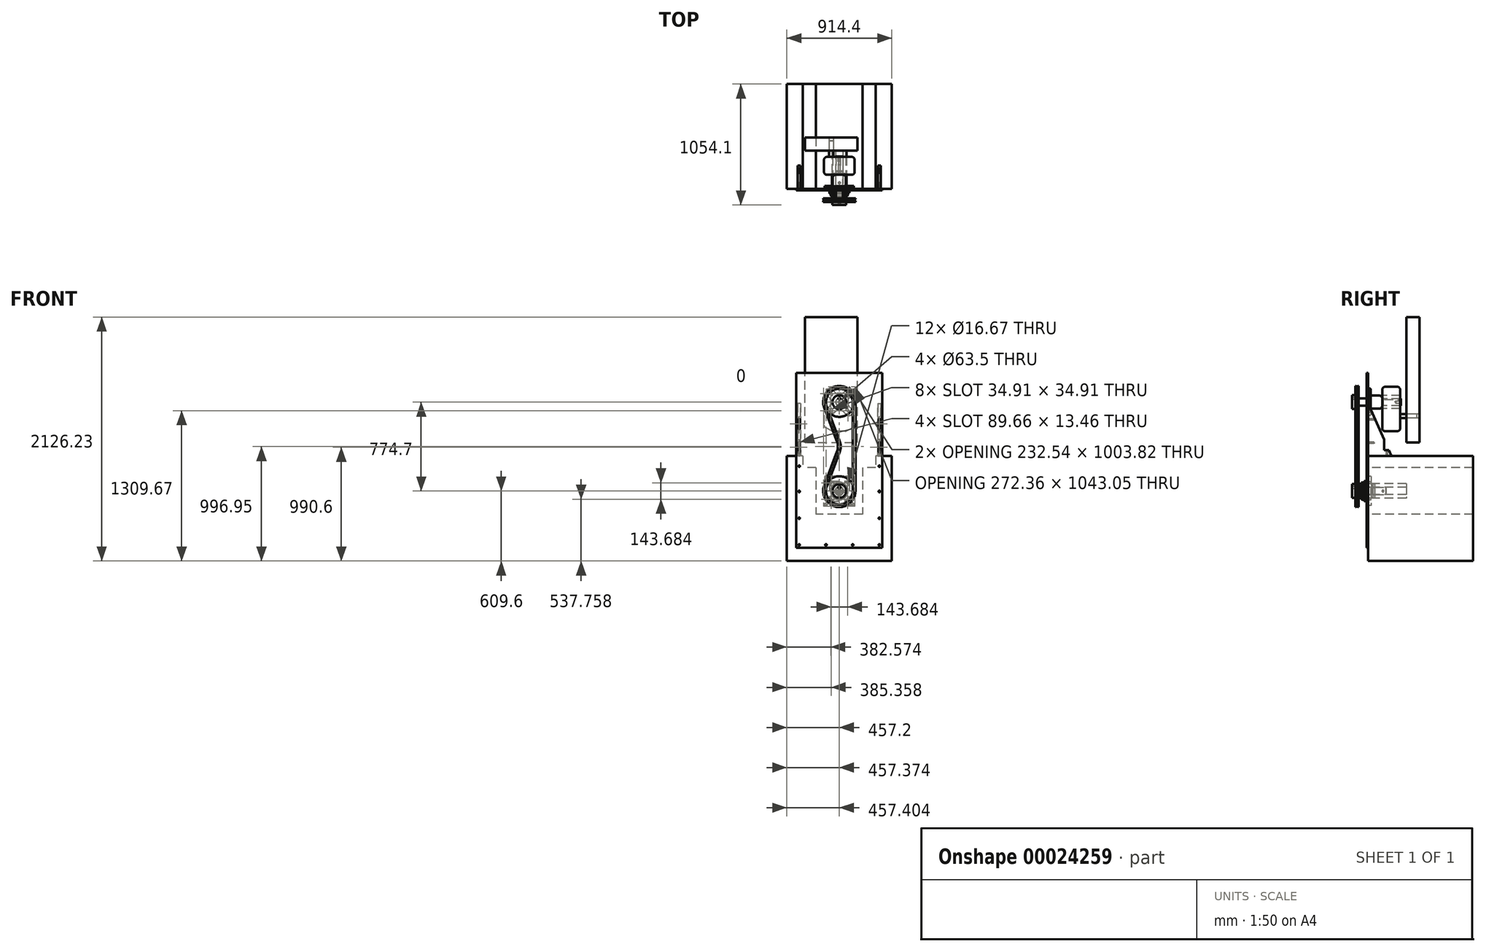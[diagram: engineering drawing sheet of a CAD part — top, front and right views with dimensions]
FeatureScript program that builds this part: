
annotation { "Feature Type Name" : "Feature", "Feature Type Description" : "" }
export const myFeature = defineFeature(function(context is Context, id is Id, definition is map)
    precondition{}
    {
        {
            var Q0;
            Q0=qCreatedBy(makeId("Front.planeOp"),FACE);
            var sketch = newSketch(context, id + "F0", { "sketchPlane" : qUnion([Q0])});
            skLineSegment(sketch, "E0.bottom", {"start": v(-374.65, 254) * mm, "end": v(374.65, 254) * mm});
            skLineSegment(sketch, "E0.top", {"start": v(-374.65, -1270) * mm, "end": v(374.65, -1270) * mm});
            skLineSegment(sketch, "E0.left", {"start": v(-374.65, 254) * mm, "end": v(-374.65, -1270) * mm});
            skLineSegment(sketch, "E0.right", {"start": v(374.65, 254) * mm, "end": v(374.65, -1270) * mm});
            skCircle(sketch, "E1", {"center": v(0, 0) * mm, "radius": 31.75 * mm});
            skCircle(sketch, "E2", {"center": v(0, -774.7) * mm, "radius": 31.75 * mm});
            skLineSegment(sketch, "E3", {"start": v(349.25, -152.4) * mm, "end": v(349.25, -228.6) * mm, "construction": true});
            skArc(sketch, "E4", {"start": v(355.98, -152.4) * mm, "mid": v(349.25, -145.67) * mm, "end": v(342.52, -152.4) * mm});
            skArc(sketch, "E5", {"start": v(342.52, -228.6) * mm, "mid": v(349.25, -235.33) * mm, "end": v(355.98, -228.6) * mm});
            skLineSegment(sketch, "E6.0", {"start": v(355.98, -152.4) * mm, "end": v(355.98, -228.6) * mm});
            skLineSegment(sketch, "E7.0", {"start": v(342.52, -152.4) * mm, "end": v(342.52, -228.6) * mm});
            skArc(sketch, "E8.0.1.0", {"start": v(355.98, -355.6) * mm, "mid": v(349.25, -348.87) * mm, "end": v(342.52, -355.6) * mm});
            skLineSegment(sketch, "E8.0.1.1", {"start": v(355.98, -355.6) * mm, "end": v(355.98, -431.8) * mm});
            skArc(sketch, "E8.0.1.2", {"start": v(342.52, -431.8) * mm, "mid": v(349.25, -438.53) * mm, "end": v(355.98, -431.8) * mm});
            skLineSegment(sketch, "E8.0.1.3", {"start": v(342.52, -355.6) * mm, "end": v(342.52, -431.8) * mm});
            skArc(sketch, "E8.1.0.0", {"start": v(-342.52, -152.4) * mm, "mid": v(-349.25, -145.67) * mm, "end": v(-355.98, -152.4) * mm});
            skLineSegment(sketch, "E8.1.0.1", {"start": v(-342.52, -152.4) * mm, "end": v(-342.52, -228.6) * mm});
            skArc(sketch, "E8.1.0.2", {"start": v(-355.98, -228.6) * mm, "mid": v(-349.25, -235.33) * mm, "end": v(-342.52, -228.6) * mm});
            skLineSegment(sketch, "E8.1.0.3", {"start": v(-355.98, -152.4) * mm, "end": v(-355.98, -228.6) * mm});
            skArc(sketch, "E8.1.1.0", {"start": v(-342.52, -355.6) * mm, "mid": v(-349.25, -348.87) * mm, "end": v(-355.98, -355.6) * mm});
            skLineSegment(sketch, "E8.1.1.1", {"start": v(-342.52, -355.6) * mm, "end": v(-342.52, -431.8) * mm});
            skArc(sketch, "E8.1.1.2", {"start": v(-355.98, -431.8) * mm, "mid": v(-349.25, -438.53) * mm, "end": v(-342.52, -431.8) * mm});
            skLineSegment(sketch, "E8.1.1.3", {"start": v(-355.98, -355.6) * mm, "end": v(-355.98, -431.8) * mm});
            skLineSegment(sketch, "E8.direction1", {"start": v(342.52, -152.4) * mm, "end": v(-355.98, -152.4) * mm, "construction": true});
            skLineSegment(sketch, "E8.direction2", {"start": v(342.52, -152.4) * mm, "end": v(342.52, -355.6) * mm, "construction": true});
            skSolve(sketch);
        }
        {
            var Q0;
            Q0=makeQuery(id+"F0.imprint","IMPRINT",FACE,{"disambiguationData":[TD([[makeQuery(id+"F0.imprint","IMPRINT",EDGE,{"derivedFrom":sQuery(id+"F0.wireOp",EDGE,"E0.bottom")}),-1.0]])]});
            extrude(context, id + "F1", {"entities" : qUnion([Q0]), "depth" : 12.7 * mm});
        }
        {
            var Q0;
            Q0=makeQuery(id+"F1.opExtrude","CAP_FACE",FACE,{"disambiguationData":[OSD([sQuery(id+"F0.wireOp",EDGE,"E0.bottom"),sQuery(id+"F0.wireOp",EDGE,"E0.top"),sQuery(id+"F0.wireOp",EDGE,"E0.left"),sQuery(id+"F0.wireOp",EDGE,"E0.right"),sQuery(id+"F0.wireOp",EDGE,"E1")])],"isStart":false});
            var sketch = newSketch(context, id + "F2", { "sketchPlane" : qUnion([Q0])});
            skCircle(sketch, "E9", {"center": v(0, 0) * mm, "radius": 92.08 * mm, "construction": true});
            skLineSegment(sketch, "E10", {"start": v(0, 0) * mm, "end": v(65.1, 65.1) * mm, "construction": true});
            skLineSegment(sketch, "E11", {"start": v(65.1, 65.1) * mm, "end": v(84.14, 84.14) * mm, "construction": true});
            skArc(sketch, "E12", {"start": v(89.76, 78.53) * mm, "mid": v(89.76, 89.76) * mm, "end": v(78.53, 89.76) * mm});
            skArc(sketch, "E13", {"start": v(59.5, 70.72) * mm, "mid": v(59.5, 59.5) * mm, "end": v(70.72, 59.5) * mm});
            skLineSegment(sketch, "E14", {"start": v(59.5, 70.72) * mm, "end": v(78.53, 89.76) * mm});
            skLineSegment(sketch, "E15", {"start": v(70.72, 59.5) * mm, "end": v(89.76, 78.53) * mm});
            skArc(sketch, "E16.1.0", {"start": v(-78.53, 89.76) * mm, "mid": v(-89.76, 89.76) * mm, "end": v(-89.76, 78.53) * mm});
            skLineSegment(sketch, "E16.1.1", {"start": v(-59.5, 70.72) * mm, "end": v(-78.53, 89.76) * mm});
            skArc(sketch, "E16.1.2", {"start": v(-70.72, 59.5) * mm, "mid": v(-59.5, 59.5) * mm, "end": v(-59.5, 70.72) * mm});
            skLineSegment(sketch, "E16.1.3", {"start": v(-70.72, 59.5) * mm, "end": v(-89.76, 78.53) * mm});
            skArc(sketch, "E16.2.0", {"start": v(-89.76, -78.53) * mm, "mid": v(-89.76, -89.76) * mm, "end": v(-78.53, -89.76) * mm});
            skLineSegment(sketch, "E16.2.1", {"start": v(-70.72, -59.5) * mm, "end": v(-89.76, -78.53) * mm});
            skArc(sketch, "E16.2.2", {"start": v(-59.5, -70.72) * mm, "mid": v(-59.5, -59.5) * mm, "end": v(-70.72, -59.5) * mm});
            skLineSegment(sketch, "E16.2.3", {"start": v(-59.5, -70.72) * mm, "end": v(-78.53, -89.76) * mm});
            skArc(sketch, "E16.3.0", {"start": v(78.53, -89.76) * mm, "mid": v(89.76, -89.76) * mm, "end": v(89.76, -78.53) * mm});
            skLineSegment(sketch, "E16.3.1", {"start": v(59.5, -70.72) * mm, "end": v(78.53, -89.76) * mm});
            skArc(sketch, "E16.3.2", {"start": v(70.72, -59.5) * mm, "mid": v(59.5, -59.5) * mm, "end": v(59.5, -70.72) * mm});
            skLineSegment(sketch, "E16.3.3", {"start": v(70.72, -59.5) * mm, "end": v(89.76, -78.53) * mm});
            skCircle(sketch, "E17.0", {"center": v(0, -774.7) * mm, "radius": 31.75 * mm});
            skCircle(sketch, "E18", {"center": v(0, -774.7) * mm, "radius": 101.6 * mm, "construction": true});
            skLineSegment(sketch, "E19", {"start": v(0, -774.7) * mm, "end": v(-71.84, -702.86) * mm, "construction": true});
            skLineSegment(sketch, "E20", {"start": v(0, -774.7) * mm, "end": v(-71.84, -846.54) * mm, "construction": true});
            skLineSegment(sketch, "E21", {"start": v(0, -774.7) * mm, "end": v(71.84, -846.54) * mm, "construction": true});
            skLineSegment(sketch, "E22", {"start": v(0, -774.7) * mm, "end": v(71.84, -702.86) * mm, "construction": true});
            skCircle(sketch, "E23", {"center": v(-71.84, -702.86) * mm, "radius": 8.33 * mm});
            skCircle(sketch, "E24", {"center": v(71.84, -702.86) * mm, "radius": 8.33 * mm});
            skCircle(sketch, "E25", {"center": v(71.84, -846.54) * mm, "radius": 8.33 * mm});
            skCircle(sketch, "E26", {"center": v(-71.84, -846.54) * mm, "radius": 8.33 * mm});
            skSolve(sketch);
        }
        {
            var Q0;
            Q0=makeQuery(id+"F2.imprint","IMPRINT",FACE,{"disambiguationData":[TD([[makeQuery(id+"F2.imprint","IMPRINT",EDGE,{"derivedFrom":sQuery(id+"F2.wireOp",EDGE,"E16.1.0")}),1.0]])]});
            var Q1;
            Q1=makeQuery(id+"F2.imprint","IMPRINT",FACE,{"disambiguationData":[TD([[makeQuery(id+"F2.imprint","IMPRINT",EDGE,{"derivedFrom":sQuery(id+"F2.wireOp",EDGE,"E12")}),1.0]])]});
            var Q2;
            Q2=makeQuery(id+"F2.imprint","IMPRINT",FACE,{"disambiguationData":[TD([[makeQuery(id+"F2.imprint","IMPRINT",EDGE,{"derivedFrom":sQuery(id+"F2.wireOp",EDGE,"E16.3.0")}),1.0]])]});
            var Q3;
            Q3=makeQuery(id+"F2.imprint","IMPRINT",FACE,{"disambiguationData":[TD([[makeQuery(id+"F2.imprint","IMPRINT",EDGE,{"derivedFrom":sQuery(id+"F2.wireOp",EDGE,"E16.2.0")}),1.0]])]});
            var Q4;
            Q4=makeQuery(id+"F2.imprint","IMPRINT",FACE,{"disambiguationData":[TD([[makeQuery(id+"F2.imprint","IMPRINT",EDGE,{"derivedFrom":sQuery(id+"F2.wireOp",EDGE,"E23")}),1.0]])]});
            var Q5;
            Q5=makeQuery(id+"F2.imprint","IMPRINT",FACE,{"disambiguationData":[TD([[makeQuery(id+"F2.imprint","IMPRINT",EDGE,{"derivedFrom":sQuery(id+"F2.wireOp",EDGE,"E24")}),1.0]])]});
            var Q6;
            Q6=makeQuery(id+"F2.imprint","IMPRINT",FACE,{"disambiguationData":[TD([[makeQuery(id+"F2.imprint","IMPRINT",EDGE,{"derivedFrom":sQuery(id+"F2.wireOp",EDGE,"E25")}),1.0]])]});
            var Q7;
            Q7=makeQuery(id+"F2.imprint","IMPRINT",FACE,{"disambiguationData":[TD([[makeQuery(id+"F2.imprint","IMPRINT",EDGE,{"derivedFrom":sQuery(id+"F2.wireOp",EDGE,"E26")}),1.0]])]});
            extrude(context, id + "F3", {"entities" : qUnion([Q0, Q1, Q2, Q3, Q4, Q5, Q6, Q7]), "operationType" : NewBodyOperationType.REMOVE, "endBound" : BoundingType.THROUGH_ALL, "oppositeDirection" : true, "depth" : 25.4 * mm});
        }
        {
            var Q0;
            Q0=makeQuery(id+"F1.opExtrude","CAP_FACE",FACE,{"disambiguationData":[OSD([sQuery(id+"F0.wireOp",EDGE,"E0.bottom"),sQuery(id+"F0.wireOp",EDGE,"E0.top"),sQuery(id+"F0.wireOp",EDGE,"E0.left"),sQuery(id+"F0.wireOp",EDGE,"E0.right"),sQuery(id+"F0.wireOp",EDGE,"E1")])],"isStart":false});
            var sketch = newSketch(context, id + "F4", { "sketchPlane" : qUnion([Q0])});
            skLineSegment(sketch, "E27", {"start": v(-349.25, -1244.6) * mm, "end": v(-349.25, -1011.68) * mm});
            skLineSegment(sketch, "E28", {"start": v(-349.25, -1011.68) * mm, "end": v(-349.25, -778.76) * mm});
            skLineSegment(sketch, "E29", {"start": v(-349.25, -778.76) * mm, "end": v(-349.25, -558.55) * mm});
            skLineSegment(sketch, "E30", {"start": v(-349.25, -1244.6) * mm, "end": v(-116.42, -1244.6) * mm});
            skLineSegment(sketch, "E31", {"start": v(-116.42, -1244.6) * mm, "end": v(116.42, -1244.6) * mm});
            skLineSegment(sketch, "E32", {"start": v(116.42, -1244.6) * mm, "end": v(349.25, -1244.6) * mm});
            skLineSegment(sketch, "E33", {"start": v(349.25, -1244.6) * mm, "end": v(349.25, -1011.68) * mm});
            skLineSegment(sketch, "E34", {"start": v(349.25, -1011.68) * mm, "end": v(349.25, -778.76) * mm});
            skLineSegment(sketch, "E35", {"start": v(349.25, -778.76) * mm, "end": v(349.25, -558.55) * mm});
            skSolve(sketch);
        }
        {
            var Q0;
            Q0=makeQuery(id+"F1.opExtrude","CAP_FACE",FACE,{"disambiguationData":[OSD([sQuery(id+"F0.wireOp",EDGE,"E0.bottom"),sQuery(id+"F0.wireOp",EDGE,"E0.top"),sQuery(id+"F0.wireOp",EDGE,"E0.left"),sQuery(id+"F0.wireOp",EDGE,"E0.right"),sQuery(id+"F0.wireOp",EDGE,"E1"),sQuery(id+"F0.wireOp",EDGE,"E2")])],"isStart":true});
            var sketch = newSketch(context, id + "F5", { "sketchPlane" : qUnion([Q0])});
            skLineSegment(sketch, "E36.bottom", {"start": v(-457.2, -469.9) * mm, "end": v(-317.5, -469.9) * mm});
            skLineSegment(sketch, "E36.top", {"start": v(-457.2, -1384.3) * mm, "end": v(457.2, -1384.3) * mm});
            skLineSegment(sketch, "E36.left", {"start": v(-457.2, -469.9) * mm, "end": v(-457.2, -1384.3) * mm});
            skLineSegment(sketch, "E36.right", {"start": v(457.2, -469.9) * mm, "end": v(457.2, -1384.3) * mm});
            skLineSegment(sketch, "E37.top", {"start": v(-317.5, -571.5) * mm, "end": v(-203.2, -571.5) * mm});
            skLineSegment(sketch, "E37.left", {"start": v(-317.5, -469.9) * mm, "end": v(-317.5, -571.5) * mm});
            skLineSegment(sketch, "E37.right", {"start": v(317.5, -469.9) * mm, "end": v(317.5, -571.5) * mm});
            skLineSegment(sketch, "E38.top", {"start": v(-203.2, -977.9) * mm, "end": v(203.2, -977.9) * mm});
            skLineSegment(sketch, "E38.left", {"start": v(-203.2, -571.5) * mm, "end": v(-203.2, -977.9) * mm});
            skLineSegment(sketch, "E38.right", {"start": v(203.2, -571.5) * mm, "end": v(203.2, -977.9) * mm});
            skCircle(sketch, "E39.0", {"center": v(0, -774.7) * mm, "radius": 31.75 * mm});
            skLineSegment(sketch, "E40.trimOffspring", {"start": v(317.5, -469.9) * mm, "end": v(457.2, -469.9) * mm});
            skLineSegment(sketch, "E41.trimOffspring", {"start": v(203.2, -571.5) * mm, "end": v(317.5, -571.5) * mm});
            skSolve(sketch);
        }
        {
            var Q0;
            Q0=sQuery(id+"F4.wireOp",VERTEX,"E35.end");
            var Q1;
            Q1=sQuery(id+"F4.wireOp",VERTEX,"E34.end");
            var Q2;
            Q2=sQuery(id+"F4.wireOp",VERTEX,"E34.start");
            var Q3;
            Q3=sQuery(id+"F4.wireOp",VERTEX,"E33.start");
            var Q4;
            Q4=sQuery(id+"F4.wireOp",VERTEX,"E32.start");
            var Q5;
            Q5=sQuery(id+"F4.wireOp",VERTEX,"E31.start");
            var Q6;
            Q6=sQuery(id+"F4.wireOp",VERTEX,"E30.start");
            var Q7;
            Q7=sQuery(id+"F4.wireOp",VERTEX,"E28.start");
            var Q8;
            Q8=sQuery(id+"F4.wireOp",VERTEX,"E29.start");
            var Q9;
            Q9=sQuery(id+"F4.wireOp",VERTEX,"E29.end");
            var Q10;
            Q10=makeQuery(id+"F1.opExtrude","SWEPT_BODY",BODY,{"disambiguationData":[OSD([sQuery(id+"F0.wireOp",EDGE,"E0.bottom"),sQuery(id+"F0.wireOp",EDGE,"E0.top"),sQuery(id+"F0.wireOp",EDGE,"E0.left"),sQuery(id+"F0.wireOp",EDGE,"E0.right"),sQuery(id+"F0.wireOp",EDGE,"E1")])]});
            var Q11;
            Q11=makeQuery(id+"FvwLGu1whnin5f6_1.opExtrude","SWEPT_BODY",BODY,{"disambiguationData":[OSD([sQuery(id+"FVkMqshP1JO17wh_1.wireOp",EDGE,"2159b873-7c23-46c0-a165-757411d00fcc.bottom"),sQuery(id+"FVkMqshP1JO17wh_1.wireOp",EDGE,"2159b873-7c23-46c0-a165-757411d00fcc.left"),sQuery(id+"FVkMqshP1JO17wh_1.wireOp",EDGE,"2159b873-7c23-46c0-a165-757411d00fcc.right"),sQuery(id+"FVkMqshP1JO17wh_1.wireOp",EDGE,"24cee0b0-9293-4e35-ae33-5d15161a7884"),sQuery(id+"FVkMqshP1JO17wh_1.wireOp",EDGE,"e78e265b-dc5b-44fe-aaf9-1faecd1ba932"),sQuery(id+"FVkMqshP1JO17wh_1.wireOp",EDGE,"51ab0597-e32d-4c84-8225-5ee1c56d9c90"),sQuery(id+"FVkMqshP1JO17wh_1.wireOp",EDGE,"ce015651-3a30-42d7-9bac-c5efad851505"),sQuery(id+"FVkMqshP1JO17wh_1.wireOp",EDGE,"805c59fc-a44f-49e7-a92e-07f28f15a35c.top"),sQuery(id+"FVkMqshP1JO17wh_1.wireOp",EDGE,"805c59fc-a44f-49e7-a92e-07f28f15a35c.left"),sQuery(id+"FVkMqshP1JO17wh_1.wireOp",EDGE,"805c59fc-a44f-49e7-a92e-07f28f15a35c.right"),sQuery(id+"FVkMqshP1JO17wh_1.wireOp",EDGE,"c6b7b8a5-442b-4015-a9d0-dc06ce9f7f00"),sQuery(id+"FVkMqshP1JO17wh_1.wireOp",EDGE,"5b3478ee-b074-467e-b26d-c07e6315da08.trimOffspring")])]});
            hole(context, id + "F6", {"style" : HoleStyle.SIMPLE, "holeDiameter" : 13.46 * mm, "endStyle" : HoleEndStyle.BLIND, "holeDepth" : 76.2 * mm, "locations" : qUnion([Q0, Q1, Q2, Q3, Q4, Q5, Q6, Q7, Q8, Q9]), "scope" : qUnion([Q10, Q11])});
        }
        {
            var Q0;
            Q0=makeQuery(id+"F5.imprint","IMPRINT",FACE,{"disambiguationData":[TD([[makeQuery(id+"F5.imprint","IMPRINT",EDGE,{"derivedFrom":sQuery(id+"F5.wireOp",EDGE,"E36.top")}),1.0]])]});
            var Q1;
            Q1=makeQuery(id+"F5.imprint","IMPRINT",FACE,{"disambiguationData":[TD([[makeQuery(id+"F5.imprint","IMPRINT",EDGE,{"derivedFrom":sQuery(id+"F5.wireOp",EDGE,"E37.top")}),-1.0]])]});
            extrude(context, id + "F7", {"entities" : qUnion([Q0, Q1]), "depth" : 914.4 * mm});
        }
        {
            var Q0;
            Q0=makeQuery(id+"F1.opExtrude","CAP_FACE",FACE,{"disambiguationData":[OSD([sQuery(id+"F0.wireOp",EDGE,"E0.bottom"),sQuery(id+"F0.wireOp",EDGE,"E0.top"),sQuery(id+"F0.wireOp",EDGE,"E0.left"),sQuery(id+"F0.wireOp",EDGE,"E0.right"),sQuery(id+"F0.wireOp",EDGE,"E1"),sQuery(id+"F0.wireOp",EDGE,"E2")])],"isStart":true});
            var sketch = newSketch(context, id + "F8", { "sketchPlane" : qUnion([Q0])});
            skLineSegment(sketch, "E42.bottom", {"start": v(-127, -647.7) * mm, "end": v(127, -647.7) * mm});
            skLineSegment(sketch, "E42.top", {"start": v(-127, -901.7) * mm, "end": v(127, -901.7) * mm});
            skLineSegment(sketch, "E42.left", {"start": v(-127, -647.7) * mm, "end": v(-127, -901.7) * mm});
            skLineSegment(sketch, "E42.right", {"start": v(127, -647.7) * mm, "end": v(127, -901.7) * mm});
            skCircle(sketch, "E43.0", {"center": v(-71.84, -702.86) * mm, "radius": 8.33 * mm});
            skCircle(sketch, "E44.0", {"center": v(0, -774.7) * mm, "radius": 31.75 * mm});
            skCircle(sketch, "E45.0", {"center": v(71.84, -702.86) * mm, "radius": 8.33 * mm});
            skCircle(sketch, "E46.0", {"center": v(71.84, -846.54) * mm, "radius": 8.33 * mm});
            skCircle(sketch, "E47.0", {"center": v(-71.84, -846.54) * mm, "radius": 8.33 * mm});
            skSolve(sketch);
        }
        {
            var Q0;
            Q0=makeQuery(id+"F8.imprint","IMPRINT",FACE,{"disambiguationData":[TD([[makeQuery(id+"F8.imprint","IMPRINT",EDGE,{"derivedFrom":sQuery(id+"F8.wireOp",EDGE,"E42.bottom")}),-1.0]])]});
            extrude(context, id + "F9", {"entities" : qUnion([Q0]), "depth" : 25.4 * mm});
        }
        {
            var Q0;
            Q0=makeQuery(id+"F1.opExtrude","CAP_FACE",FACE,{"disambiguationData":[OSD([sQuery(id+"F0.wireOp",EDGE,"E0.bottom"),sQuery(id+"F0.wireOp",EDGE,"E0.top"),sQuery(id+"F0.wireOp",EDGE,"E0.left"),sQuery(id+"F0.wireOp",EDGE,"E0.right"),sQuery(id+"F0.wireOp",EDGE,"E1"),sQuery(id+"F0.wireOp",EDGE,"E2")])],"isStart":false});
            var sketch = newSketch(context, id + "F10", { "sketchPlane" : qUnion([Q0])});
            skCircle(sketch, "E48.0", {"center": v(0, -774.7) * mm, "radius": 31.75 * mm});
            skCircle(sketch, "E49", {"center": v(0, -774.7) * mm, "radius": 30.92 * mm});
            skSolve(sketch);
        }
        {
            var Q0;
            Q0=makeQuery(id+"F10.imprint","IMPRINT",FACE,{"disambiguationData":[TD([[makeQuery(id+"F10.imprint","IMPRINT",EDGE,{"derivedFrom":sQuery(id+"F10.wireOp",EDGE,"E49")}),1.0]])]});
            extrude(context, id + "F11", {"entities" : qUnion([Q0]), "depth" : 127 * mm});
        }
        {
            var Q0;
            Q0=makeQuery(id+"F1.opExtrude","SWEPT_FACE",FACE,{"disambiguationData":[OSD([sQuery(id+"F0.wireOp",EDGE,"E0.top")])]});
            cPlane(context, id + "F12", {"entities" : qUnion([Q0]), "cplaneType" : CPlaneType.OFFSET, "offset" : 526.26 * mm, "oppositeDirection" : true, "width" : 152.4 * mm, "height" : 152.4 * mm});
        }
        {
            var Q0;
            Q0=qCreatedBy(id+"F12.planeOp",FACE);
            var sketch = newSketch(context, id + "F13", { "sketchPlane" : qUnion([Q0])});
            skLineSegment(sketch, "E50", {"start": v(-30.92, 12.7) * mm, "end": v(-30.92, 165.1) * mm});
            skLineSegment(sketch, "E51", {"start": v(30.92, 165.1) * mm, "end": v(30.92, 12.7) * mm});
            skLineSegment(sketch, "E52.bottom", {"start": v(7.94, 165.1) * mm, "end": v(-7.94, 165.1) * mm});
            skLineSegment(sketch, "E52.left", {"start": v(7.94, 165.1) * mm, "end": v(7.94, 88.9) * mm});
            skLineSegment(sketch, "E52.right", {"start": v(-7.94, 165.1) * mm, "end": v(-7.94, 88.9) * mm});
            skArc(sketch, "E53", {"start": v(-7.94, 88.9) * mm, "mid": v(0, 80.96) * mm, "end": v(7.94, 88.9) * mm});
            skSolve(sketch);
        }
        {
            var Q0;
            Q0=makeQuery(id+"F13.imprint","IMPRINT",FACE,{"disambiguationData":[TD([[makeQuery(id+"F13.imprint","IMPRINT",EDGE,{"derivedFrom":sQuery(id+"F13.wireOp",EDGE,"E52.bottom")}),1.0]])]});
            extrude(context, id + "F14", {"entities" : qUnion([Q0]), "operationType" : NewBodyOperationType.REMOVE, "depth" : 8.3 * mm});
        }
        {
            var Q0;
            Q0=makeQuery(id+"F11.opExtrude","CAP_FACE",FACE,{"disambiguationData":[OSD([sQuery(id+"F10.wireOp",EDGE,"E49")])],"isStart":true});
            extrude(context, id + "F15", {"entities" : qUnion([Q0]), "operationType" : NewBodyOperationType.ADD, "depth" : 168.27 * mm});
        }
        {
            var Q0;
            Q0=makeQuery(id+"F9.opExtrude","SWEPT_FACE",FACE,{"disambiguationData":[OSD([sQuery(id+"F8.wireOp",EDGE,"E42.left")])]});
            cPlane(context, id + "F16", {"entities" : qUnion([Q0]), "cplaneType" : CPlaneType.OFFSET, "offset" : 0 * mm, "width" : 152.4 * mm, "height" : 152.4 * mm});
        }
        {
            var Q0;
            Q0=makeQuery(id+"F9.opExtrude","SWEPT_FACE",FACE,{"disambiguationData":[OSD([sQuery(id+"F8.wireOp",EDGE,"E42.bottom")])]});
            cPlane(context, id + "F17", {"entities" : qUnion([Q0]), "cplaneType" : CPlaneType.OFFSET, "offset" : 0 * mm, "width" : 152.4 * mm, "height" : 152.4 * mm});
        }
        {
            var Q0;
            Q0=makeQuery(id+"F9.opExtrude","CAP_FACE",FACE,{"disambiguationData":[OSD([sQuery(id+"F8.wireOp",EDGE,"E42.bottom"),sQuery(id+"F8.wireOp",EDGE,"E42.top"),sQuery(id+"F8.wireOp",EDGE,"E42.left"),sQuery(id+"F8.wireOp",EDGE,"E42.right"),sQuery(id+"F8.wireOp",EDGE,"E43.0"),sQuery(id+"F8.wireOp",EDGE,"E44.0"),sQuery(id+"F8.wireOp",EDGE,"E45.0"),sQuery(id+"F8.wireOp",EDGE,"E46.0"),sQuery(id+"F8.wireOp",EDGE,"E47.0")])],"isStart":false});
            cPlane(context, id + "F18", {"entities" : qUnion([Q0]), "cplaneType" : CPlaneType.OFFSET, "offset" : 3.17 * mm, "width" : 152.4 * mm, "height" : 152.4 * mm});
        }
        {
            var Q0;
            Q0=qCreatedBy(id+"F18.planeOp",FACE);
            var sketch = newSketch(context, id + "F19", { "sketchPlane" : qUnion([Q0])});
            skCircle(sketch, "E54", {"center": v(0, -774.7) * mm, "radius": 63.5 * mm});
            skCircle(sketch, "E55.0", {"center": v(0, -774.7) * mm, "radius": 31.75 * mm});
            skSolve(sketch);
        }
        {
            var Q0;
            Q0=makeQuery(id+"F19.imprint","IMPRINT",FACE,{"disambiguationData":[TD([[makeQuery(id+"F19.imprint","IMPRINT",EDGE,{"derivedFrom":sQuery(id+"F19.wireOp",EDGE,"E54")}),1.0]])]});
            extrude(context, id + "F20", {"entities" : qUnion([Q0]), "depth" : 304.8 * mm});
        }
        {
            var Q0;
            Q0=qCreatedBy(id+"F17.planeOp",FACE);
            var sketch = newSketch(context, id + "F21", { "sketchPlane" : qUnion([Q0])});
            skLineSegment(sketch, "E56", {"start": v(0, 0) * mm, "end": v(0, 53.98) * mm, "construction": true});
            skLineSegment(sketch, "E57.0", {"start": v(-63.5, 28.58) * mm, "end": v(63.5, 28.58) * mm});
            skSolve(sketch);
        }
        {
            var Q0;
            Q0=qCreatedBy(id+"F16.planeOp",FACE);
            var sketch = newSketch(context, id + "F22", { "sketchPlane" : qUnion([Q0])});
            skLineSegment(sketch, "E58.0", {"start": v(28.58, -711.2) * mm, "end": v(28.58, -838.2) * mm});
            skLineSegment(sketch, "E59", {"start": v(28.58, -774.7) * mm, "end": v(130.18, -774.7) * mm});
            skSolve(sketch);
        }
        {
            var Q0;
            Q0=makeQuery(id+"F1.opExtrude","CAP_FACE",FACE,{"disambiguationData":[OSD([sQuery(id+"F0.wireOp",EDGE,"E0.bottom"),sQuery(id+"F0.wireOp",EDGE,"E0.top"),sQuery(id+"F0.wireOp",EDGE,"E0.left"),sQuery(id+"F0.wireOp",EDGE,"E0.right"),sQuery(id+"F0.wireOp",EDGE,"E1"),sQuery(id+"F0.wireOp",EDGE,"E2")])],"isStart":false});
            var sketch = newSketch(context, id + "F23", { "sketchPlane" : qUnion([Q0])});
            skLineSegment(sketch, "E60.bottom", {"start": v(-87.5, -687.2) * mm, "end": v(87.5, -687.2) * mm});
            skLineSegment(sketch, "E60.top", {"start": v(-87.5, -862.2) * mm, "end": v(87.5, -862.2) * mm});
            skLineSegment(sketch, "E60.left", {"start": v(-87.5, -687.2) * mm, "end": v(-87.5, -862.2) * mm});
            skLineSegment(sketch, "E60.right", {"start": v(87.5, -687.2) * mm, "end": v(87.5, -862.2) * mm});
            skCircle(sketch, "E61.0", {"center": v(0, -774.7) * mm, "radius": 31.75 * mm});
            skSolve(sketch);
        }
        {
            var Q0;
            Q0=makeQuery(id+"F23.imprint","IMPRINT",FACE,{"disambiguationData":[TD([[makeQuery(id+"F23.imprint","IMPRINT",EDGE,{"derivedFrom":sQuery(id+"F23.wireOp",EDGE,"E60.bottom")}),-1.0]])]});
            extrude(context, id + "F24", {"entities" : qUnion([Q0]), "depth" : 18 * mm});
        }
        {
            var Q0;
            Q0=makeQuery(id+"F24.opExtrude","SWEPT_EDGE",EDGE,{"disambiguationData":[OSD([sQuery(id+"F23.wireOp",EDGE,"E60.bottom"),sQuery(id+"F23.wireOp",EDGE,"E60.right")])]});
            var Q1;
            Q1=makeQuery(id+"F24.opExtrude","SWEPT_EDGE",EDGE,{"disambiguationData":[OSD([sQuery(id+"F23.wireOp",EDGE,"E60.bottom"),sQuery(id+"F23.wireOp",EDGE,"E60.left")])]});
            var Q2;
            Q2=makeQuery(id+"F24.opExtrude","SWEPT_EDGE",EDGE,{"disambiguationData":[OSD([sQuery(id+"F23.wireOp",EDGE,"E60.top"),sQuery(id+"F23.wireOp",EDGE,"E60.right")])]});
            var Q3;
            Q3=makeQuery(id+"F24.opExtrude","SWEPT_EDGE",EDGE,{"disambiguationData":[OSD([sQuery(id+"F23.wireOp",EDGE,"E60.top"),sQuery(id+"F23.wireOp",EDGE,"E60.left")])]});
            fillet(context, id + "F25", {"entities" : qUnion([Q0, Q1, Q2, Q3]), "radius" : 15.88 * mm, "tangentPropagation" : true, "allowEdgeOverflow" : false});
        }
        {
            var Q0;
            Q0=makeQuery(id+"F24.opExtrude","CAP_FACE",FACE,{"disambiguationData":[OSD([sQuery(id+"F2.wireOp",EDGE,"E23"),sQuery(id+"F2.wireOp",EDGE,"E24"),sQuery(id+"F2.wireOp",EDGE,"E25"),sQuery(id+"F2.wireOp",EDGE,"E26"),sQuery(id+"F23.wireOp",EDGE,"E60.bottom"),sQuery(id+"F23.wireOp",EDGE,"E60.top"),sQuery(id+"F23.wireOp",EDGE,"E60.left"),sQuery(id+"F23.wireOp",EDGE,"E60.right"),sQuery(id+"F23.wireOp",EDGE,"E61.0")])],"isStart":false});
            var sketch = newSketch(context, id + "F26", { "sketchPlane" : qUnion([Q0])});
            skCircle(sketch, "E62", {"center": v(0, -774.7) * mm, "radius": 76.2 * mm});
            skCircle(sketch, "E63.0", {"center": v(0, -774.7) * mm, "radius": 31.75 * mm});
            skSolve(sketch);
        }
        {
            var Q0;
            Q0=makeQuery(id+"F24.opExtrude","CAP_FACE",FACE,{"disambiguationData":[OSD([sQuery(id+"F2.wireOp",EDGE,"E23"),sQuery(id+"F2.wireOp",EDGE,"E24"),sQuery(id+"F2.wireOp",EDGE,"E25"),sQuery(id+"F2.wireOp",EDGE,"E26"),sQuery(id+"F23.wireOp",EDGE,"E60.bottom"),sQuery(id+"F23.wireOp",EDGE,"E60.top"),sQuery(id+"F23.wireOp",EDGE,"E60.left"),sQuery(id+"F23.wireOp",EDGE,"E60.right"),sQuery(id+"F23.wireOp",EDGE,"E61.0")])],"isStart":false});
            var sketch = newSketch(context, id + "F27", { "sketchPlane" : qUnion([Q0])});
            skLineSegment(sketch, "E64.0.0", {"start": v(71.63, -687.2) * mm, "end": v(-71.63, -687.2) * mm});
            skArc(sketch, "E64.0.1", {"start": v(-71.63, -687.2) * mm, "mid": v(-82.85, -691.85) * mm, "end": v(-87.5, -703.08) * mm});
            skLineSegment(sketch, "E64.0.2", {"start": v(-87.5, -703.08) * mm, "end": v(-87.5, -846.33) * mm});
            skArc(sketch, "E64.0.3", {"start": v(-87.5, -846.33) * mm, "mid": v(-82.85, -857.55) * mm, "end": v(-71.63, -862.2) * mm});
            skLineSegment(sketch, "E64.0.4", {"start": v(-71.63, -862.2) * mm, "end": v(71.62, -862.2) * mm});
            skArc(sketch, "E64.0.5", {"start": v(71.62, -862.2) * mm, "mid": v(82.85, -857.55) * mm, "end": v(87.5, -846.33) * mm});
            skLineSegment(sketch, "E64.0.6", {"start": v(87.5, -846.33) * mm, "end": v(87.5, -703.08) * mm});
            skArc(sketch, "E64.0.7", {"start": v(87.5, -703.08) * mm, "mid": v(82.85, -691.85) * mm, "end": v(71.63, -687.2) * mm});
            skArc(sketch, "E65", {"start": v(-62.52, -690.07) * mm, "mid": v(-82.85, -691.85) * mm, "end": v(-84.63, -712.18) * mm});
            skArc(sketch, "E66", {"start": v(84.63, -712.18) * mm, "mid": v(82.6, -691.61) * mm, "end": v(61.98, -690.47) * mm});
            skArc(sketch, "E67", {"start": v(62.52, -859.33) * mm, "mid": v(82.85, -857.55) * mm, "end": v(84.63, -837.22) * mm});
            skArc(sketch, "E68", {"start": v(-84.63, -837.22) * mm, "mid": v(-82.85, -857.55) * mm, "end": v(-62.52, -859.33) * mm});
            skCircle(sketch, "E69.0", {"center": v(0, -774.7) * mm, "radius": 31.75 * mm});
            skCircle(sketch, "E70", {"center": v(0, -774.7) * mm, "radius": 50.8 * mm});
            skLineSegment(sketch, "E71", {"start": v(-84.63, -712.18) * mm, "end": v(-49.33, -762.59) * mm});
            skLineSegment(sketch, "E72", {"start": v(-62.52, -690.07) * mm, "end": v(-12.11, -725.37) * mm});
            skLineSegment(sketch, "E73", {"start": v(15.24, -726.24) * mm, "end": v(61.98, -690.47) * mm});
            skLineSegment(sketch, "E74", {"start": v(84.63, -712.18) * mm, "end": v(49.33, -762.59) * mm});
            skLineSegment(sketch, "E75", {"start": v(49.33, -786.81) * mm, "end": v(84.63, -837.22) * mm});
            skLineSegment(sketch, "E76", {"start": v(12.11, -824.03) * mm, "end": v(62.52, -859.33) * mm});
            skLineSegment(sketch, "E77", {"start": v(-12.11, -824.03) * mm, "end": v(-62.52, -859.33) * mm});
            skLineSegment(sketch, "E78", {"start": v(-84.63, -837.22) * mm, "end": v(-49.33, -786.81) * mm});
            skSolve(sketch);
        }
        {
            var Q0;
            {var subQ1=sQuery(id+"F27.wireOp",EDGE,"E71");Q0=makeQuery(id+"F27.imprint","IMPRINT",FACE,{"disambiguationData":[TD([[makeQuery(id+"F27.imprint","IMPRINT",EDGE,{"derivedFrom":subQ1}),1.0]])]});}
            var Q1;
            {var subQ1=sQuery(id+"F27.wireOp",EDGE,"E73");Q1=makeQuery(id+"F27.imprint","IMPRINT",FACE,{"disambiguationData":[TD([[makeQuery(id+"F27.imprint","IMPRINT",EDGE,{"derivedFrom":subQ1}),-1.0]])]});}
            var Q2;
            {var subQ1=sQuery(id+"F27.wireOp",EDGE,"E75");Q2=makeQuery(id+"F27.imprint","IMPRINT",FACE,{"disambiguationData":[TD([[makeQuery(id+"F27.imprint","IMPRINT",EDGE,{"derivedFrom":subQ1}),-1.0]])]});}
            var Q3;
            {var subQ1=sQuery(id+"F27.wireOp",EDGE,"E77");Q3=makeQuery(id+"F27.imprint","IMPRINT",FACE,{"disambiguationData":[TD([[makeQuery(id+"F27.imprint","IMPRINT",EDGE,{"derivedFrom":subQ1}),-1.0]])]});}
            extrude(context, id + "F28", {"entities" : qUnion([Q0, Q1, Q2, Q3]), "operationType" : NewBodyOperationType.ADD, "depth" : 3.17 * mm});
        }
        {
            var Q0;
            Q0=makeQuery(id+"F26.imprint","IMPRINT",FACE,{"disambiguationData":[TD([[makeQuery(id+"F26.imprint","IMPRINT",EDGE,{"derivedFrom":sQuery(id+"F26.wireOp",EDGE,"E62")}),1.0]])]});
            extrude(context, id + "F29", {"entities" : qUnion([Q0]), "operationType" : NewBodyOperationType.ADD, "depth" : 30 * mm});
        }
        {
            var Q0;
            Q0=makeQuery(id+"F29.opExtrude","CAP_EDGE",EDGE,{"disambiguationData":[OSD([sQuery(id+"F26.wireOp",EDGE,"E62")])],"isStart":false});
            chamfer(context, id + "F30", {"entities" : qUnion([Q0]), "chamferType" : ChamferType.OFFSET_ANGLE, "width" : 19.05 * mm, "oppositeDirection" : true, "angle" : 10 * degree, "tangentPropagation" : true});
        }
        {
            var Q0;
            Q0=makeQuery(id+"F29.opExtrude","CAP_FACE",FACE,{"disambiguationData":[OSD([sQuery(id+"F26.wireOp",EDGE,"E62"),sQuery(id+"F26.wireOp",EDGE,"6657c57f-e435-4148-895d-80a6e9c333fb")])],"isStart":false});
            var sketch = newSketch(context, id + "F31", { "sketchPlane" : qUnion([Q0])});
            skCircle(sketch, "E79", {"center": v(0, -774.7) * mm, "radius": 37.72 * mm});
            skCircle(sketch, "E80.0", {"center": v(0, -774.7) * mm, "radius": 31.75 * mm});
            skSolve(sketch);
        }
        {
            var Q0;
            Q0=makeQuery(id+"F31.imprint","IMPRINT",FACE,{"disambiguationData":[TD([[makeQuery(id+"F31.imprint","IMPRINT",EDGE,{"derivedFrom":sQuery(id+"F31.wireOp",EDGE,"E79")}),1.0]])]});
            extrude(context, id + "F32", {"entities" : qUnion([Q0]), "operationType" : NewBodyOperationType.ADD, "depth" : 20.7 * mm});
        }
        {
            var Q0;
            Q0=makeQuery(id+"F11.opExtrude","CAP_FACE",FACE,{"disambiguationData":[OSD([sQuery(id+"F10.wireOp",EDGE,"E49")])],"isStart":false});
            cPlane(context, id + "F33", {"entities" : qUnion([Q0]), "cplaneType" : CPlaneType.OFFSET, "offset" : 0 * mm, "oppositeDirection" : true, "width" : 152.4 * mm, "height" : 152.4 * mm});
        }
        {
            var Q0;
            Q0=qCreatedBy(id+"F33.planeOp",FACE);
            var sketch = newSketch(context, id + "F34", { "sketchPlane" : qUnion([Q0])});
            skArc(sketch, "E81.0", {"start": v(-7.94, -744.81) * mm, "mid": v(0, -805.62) * mm, "end": v(7.94, -744.81) * mm});
            skCircle(sketch, "E82", {"center": v(0, -774.7) * mm, "radius": 30.92 * mm});
            skCircle(sketch, "E83", {"center": v(0, -774.7) * mm, "radius": 60.33 * mm});
            skLineSegment(sketch, "E84", {"start": v(-7.94, -744.81) * mm, "end": v(-7.94, -736.16) * mm});
            skLineSegment(sketch, "E85", {"start": v(-7.94, -736.16) * mm, "end": v(7.94, -736.16) * mm});
            skLineSegment(sketch, "E86", {"start": v(7.94, -744.81) * mm, "end": v(7.94, -736.16) * mm});
            skSolve(sketch);
        }
        {
            var Q0;
            Q0=makeQuery(id+"F34.imprint","IMPRINT",FACE,{"disambiguationData":[TD([[makeQuery(id+"F34.imprint","IMPRINT",EDGE,{"derivedFrom":sQuery(id+"F34.wireOp",EDGE,"E83")}),1.0]])]});
            extrude(context, id + "F35", {"entities" : qUnion([Q0]), "oppositeDirection" : true, "depth" : 36.2 * mm});
        }
        {
            var Q0;
            Q0=makeQuery(id+"F35.opExtrude","CAP_FACE",FACE,{"disambiguationData":[OSD([sQuery(id+"F34.wireOp",EDGE,"E82"),sQuery(id+"F34.wireOp",EDGE,"E83"),sQuery(id+"F34.wireOp",EDGE,"E84"),sQuery(id+"F34.wireOp",EDGE,"E85"),sQuery(id+"F34.wireOp",EDGE,"E86")])],"isStart":false});
            var sketch = newSketch(context, id + "F36", { "sketchPlane" : qUnion([Q0])});
            skArc(sketch, "E87.0", {"start": v(7.94, -744.81) * mm, "mid": v(0, -805.62) * mm, "end": v(-7.94, -744.81) * mm});
            skCircle(sketch, "E88", {"center": v(0, -774.7) * mm, "radius": 30.92 * mm});
            skCircle(sketch, "E89", {"center": v(0, -774.7) * mm, "radius": 128.45 * mm});
            skSolve(sketch);
        }
        {
            var Q0;
            Q0=makeQuery(id+"F36.imprint","IMPRINT",FACE,{"disambiguationData":[TD([[makeQuery(id+"F36.imprint","IMPRINT",EDGE,{"derivedFrom":sQuery(id+"F36.wireOp",EDGE,"E89")}),1.0]])]});
            var Q1;
            Q1=makeQuery(id+"F36.imprint","IMPRINT",FACE,{"disambiguationData":[TD([[makeQuery(id+"F36.imprint","IMPRINT",EDGE,{"disambiguationData":[OD(1.0)],"derivedFrom":sQuery(id+"F36.wireOp",EDGE,"E88")}),1.0]])]});
            extrude(context, id + "F37", {"entities" : qUnion([Q0, Q1]), "operationType" : NewBodyOperationType.ADD, "depth" : 14.6 * mm});
        }
        {
            var Q0;
            Q0=qCreatedBy(makeId("Right.planeOp"),FACE);
            var sketch = newSketch(context, id + "F38", { "sketchPlane" : qUnion([Q0])});
            skLineSegment(sketch, "E90.top", {"start": v(-139.7, 30.92) * mm, "end": v(0, 30.92) * mm});
            skLineSegment(sketch, "E90.left", {"start": v(-139.7, 0) * mm, "end": v(-139.7, 30.92) * mm});
            skLineSegment(sketch, "E91.top", {"start": v(0, 34.99) * mm, "end": v(78.74, 34.99) * mm});
            skLineSegment(sketch, "E92.bottom", {"start": v(135.04, 31.05) * mm, "end": v(285.24, 31.05) * mm});
            skLineSegment(sketch, "E92.right", {"start": v(285.24, 31.05) * mm, "end": v(285.24, 0) * mm});
            skLineSegment(sketch, "E93", {"start": v(-139.7, 0) * mm, "end": v(285.24, 0) * mm});
            skLineSegment(sketch, "E94", {"start": v(0, 34.99) * mm, "end": v(0, 30.92) * mm});
            skLineSegment(sketch, "E95", {"start": v(78.74, 34.99) * mm, "end": v(135.04, 31.05) * mm});
            skSolve(sketch);
        }
        {
            var Q0;
            Q0=makeQuery(id+"F38.imprint","IMPRINT",FACE,{"disambiguationData":[TD([[makeQuery(id+"F38.imprint","IMPRINT",EDGE,{"derivedFrom":sQuery(id+"F38.wireOp",EDGE,"E90.top")}),-1.0]])]});
            var Q1;
            Q1=sQuery(id+"F38.wireOp",EDGE,"E93");
            revolve(context, id + "F39", {"entities" : qUnion([Q0]), "axis" : qUnion([Q1]), "revolveType" : RevolveType.FULL});
        }
        {
            var Q0;
            Q0=makeQuery(id+"F1.opExtrude","SWEPT_FACE",FACE,{"disambiguationData":[OSD([sQuery(id+"F0.wireOp",EDGE,"E0.bottom")])]});
            cPlane(context, id + "F40", {"entities" : qUnion([Q0]), "cplaneType" : CPlaneType.OFFSET, "offset" : 223.04 * mm, "oppositeDirection" : true, "width" : 152.4 * mm, "height" : 152.4 * mm});
        }
        {
            var Q0;
            Q0=qCreatedBy(id+"F40.planeOp",FACE);
            var sketch = newSketch(context, id + "F41", { "sketchPlane" : qUnion([Q0])});
            skArc(sketch, "E96", {"start": v(7.94, -88.9) * mm, "mid": v(0, -80.96) * mm, "end": v(-7.94, -88.9) * mm});
            skLineSegment(sketch, "E97", {"start": v(-7.94, -88.9) * mm, "end": v(-7.94, -165.1) * mm});
            skLineSegment(sketch, "E98", {"start": v(7.94, -88.9) * mm, "end": v(7.94, -165.1) * mm});
            skLineSegment(sketch, "E99", {"start": v(-7.94, -165.1) * mm, "end": v(7.94, -165.1) * mm});
            skLineSegment(sketch, "E100.0", {"start": v(30.92, -139.7) * mm, "end": v(-30.92, -139.7) * mm});
            skSolve(sketch);
        }
        {
            var Q0;
            Q0=makeQuery(id+"F41.imprint","IMPRINT",FACE,{"disambiguationData":[TD([[makeQuery(id+"F41.imprint","IMPRINT",EDGE,{"derivedFrom":sQuery(id+"F41.wireOp",EDGE,"E96")}),1.0]])]});
            extrude(context, id + "F42", {"entities" : qUnion([Q0]), "operationType" : NewBodyOperationType.REMOVE, "oppositeDirection" : true, "depth" : 8.28 * mm});
        }
        {
            var Q0;
            Q0=makeQuery(id+"F39.opRevolve","SWEPT_FACE",FACE,{"disambiguationData":[OSD([sQuery(id+"F38.wireOp",EDGE,"E92.right")])]});
            var sketch = newSketch(context, id + "F43", { "sketchPlane" : qUnion([Q0])});
            skCircle(sketch, "E101.0", {"center": v(0, 0) * mm, "radius": 31.05 * mm});
            skSolve(sketch);
        }
        {
            var Q0;
            Q0=sQuery(id+"F43.wireOp",VERTEX,"E101.0.center");
            var Q1;
            Q1=makeQuery(id+"F39.opRevolve","SWEPT_BODY",BODY,{"disambiguationData":[OSD([sQuery(id+"F38.wireOp",EDGE,"E90.top"),sQuery(id+"F38.wireOp",EDGE,"E90.left"),sQuery(id+"F38.wireOp",EDGE,"E91.top"),sQuery(id+"F38.wireOp",EDGE,"76c26d02-83df-4411-9bb0-874c510d0430"),sQuery(id+"F38.wireOp",EDGE,"E92.bottom"),sQuery(id+"F38.wireOp",EDGE,"E92.right"),sQuery(id+"F38.wireOp",EDGE,"E93"),sQuery(id+"F38.wireOp",EDGE,"E94")])]});
            hole(context, id + "F44", {"style" : HoleStyle.SIMPLE, "holeDiameter" : 20.04 * mm, "endStyle" : HoleEndStyle.BLIND, "holeDepth" : 44.45 * mm, "locations" : qUnion([Q0]), "scope" : qUnion([Q1])});
        }
        {
            var Q0;
            Q0=makeQuery(id+"F39.opRevolve","SWEPT_FACE",FACE,{"disambiguationData":[OSD([sQuery(id+"F38.wireOp",EDGE,"E90.left")])]});
            cPlane(context, id + "F45", {"entities" : qUnion([Q0]), "cplaneType" : CPlaneType.OFFSET, "offset" : 0 * mm, "oppositeDirection" : true, "width" : 152.4 * mm, "height" : 152.4 * mm});
        }
        {
            var Q0;
            Q0=qCreatedBy(id+"F45.planeOp",FACE);
            var sketch = newSketch(context, id + "F46", { "sketchPlane" : qUnion([Q0])});
            skCircle(sketch, "E102", {"center": v(0, 0) * mm, "radius": 60.33 * mm});
            skArc(sketch, "E103.0", {"start": v(-7.94, 29.89) * mm, "mid": v(0, -30.92) * mm, "end": v(7.94, 29.89) * mm});
            skLineSegment(sketch, "E104.0.1", {"start": v(-7.94, 22.68) * mm, "end": v(7.94, 22.68) * mm});
            skLineSegment(sketch, "E104.0.3", {"start": v(-7.94, 22.68) * mm, "end": v(7.94, 22.68) * mm});
            skLineSegment(sketch, "E105.0.1", {"start": v(-7.94, 29.89) * mm, "end": v(-7.94, 22.68) * mm});
            skLineSegment(sketch, "E105.0.3", {"start": v(-7.94, 22.68) * mm, "end": v(-7.94, 29.89) * mm});
            skLineSegment(sketch, "E106.0", {"start": v(7.94, 22.68) * mm, "end": v(7.94, 29.89) * mm});
            skLineSegment(sketch, "E107.top", {"start": v(-7.94, 38.55) * mm, "end": v(7.94, 38.55) * mm});
            skLineSegment(sketch, "E107.left", {"start": v(-7.94, 29.89) * mm, "end": v(-7.94, 38.55) * mm});
            skLineSegment(sketch, "E107.right", {"start": v(7.94, 29.89) * mm, "end": v(7.94, 38.55) * mm});
            skSolve(sketch);
        }
        {
            var Q0;
            Q0=makeQuery(id+"F46.imprint","IMPRINT",FACE,{"disambiguationData":[TD([[makeQuery(id+"F46.imprint","IMPRINT",EDGE,{"derivedFrom":sQuery(id+"F46.wireOp",EDGE,"E102")}),1.0]])]});
            extrude(context, id + "F47", {"entities" : qUnion([Q0]), "oppositeDirection" : true, "depth" : 36.2 * mm});
        }
        {
            var Q0;
            Q0=makeQuery(id+"F47.opExtrude","CAP_FACE",FACE,{"disambiguationData":[OSD([sQuery(id+"F46.wireOp",EDGE,"837d0a8e-7aea-41cf-886a-b62b43243ce0"),sQuery(id+"F46.wireOp",EDGE,"E102"),sQuery(id+"F46.wireOp",EDGE,"d060f684-caa2-42fc-b72d-14a0c2717916"),sQuery(id+"F46.wireOp",EDGE,"17672764-d84c-446f-9bef-e2111f265863"),sQuery(id+"F46.wireOp",EDGE,"33cdaa7a-9be0-4ddf-9e29-9c811c9cda73")])],"isStart":false});
            var sketch = newSketch(context, id + "F48", { "sketchPlane" : qUnion([Q0])});
            skCircle(sketch, "E108", {"center": v(0, 0) * mm, "radius": 128.45 * mm});
            skSolve(sketch);
        }
        {
            var Q0;
            Q0=makeQuery(id+"F48.imprint","IMPRINT",FACE,{"disambiguationData":[TD([[makeQuery(id+"F48.imprint","IMPRINT",EDGE,{"derivedFrom":sQuery(id+"F48.wireOp",EDGE,"E108")}),1.0]])]});
            var Q1;
            Q1=makeQuery(id+"F48.imprint","IMPRINT",FACE,{"disambiguationData":[TD([[makeQuery(id+"F48.imprint","IMPRINT",EDGE,{"derivedFrom":makeQuery(id+"F47.opExtrude","CAP_EDGE",EDGE,{"disambiguationData":[OSD([sQuery(id+"F46.wireOp",EDGE,"E102")])],"isStart":false})}),-1.0]])]});
            extrude(context, id + "F49", {"entities" : qUnion([Q0, Q1]), "operationType" : NewBodyOperationType.ADD, "depth" : 14.6 * mm});
        }
        {
            var Q0;
            Q0=makeQuery(id+"F1.opExtrude","SWEPT_FACE",FACE,{"disambiguationData":[OSD([sQuery(id+"F0.wireOp",EDGE,"E0.right")])]});
            cPlane(context, id + "F50", {"entities" : qUnion([Q0]), "cplaneType" : CPlaneType.OFFSET, "offset" : 374.65 * mm, "oppositeDirection" : true, "width" : 152.4 * mm, "height" : 152.4 * mm});
        }
        {
            var Q0;
            Q0=qCreatedBy(id+"F50.planeOp",FACE);
            var sketch = newSketch(context, id + "F51", { "sketchPlane" : qUnion([Q0])});
            skLineSegment(sketch, "E109.top", {"start": v(-104.14, 136.39) * mm, "end": v(-88.26, 136.39) * mm});
            skLineSegment(sketch, "E110.bottom", {"start": v(-104.14, 140.45) * mm, "end": v(-111.93, 140.45) * mm});
            skLineSegment(sketch, "E110.top", {"start": v(-104.14, 116.45) * mm, "end": v(-111.93, 116.45) * mm});
            skLineSegment(sketch, "E110.left", {"start": v(-104.14, 140.45) * mm, "end": v(-104.14, 136.39) * mm});
            skLineSegment(sketch, "E110.right", {"start": v(-111.93, 140.45) * mm, "end": v(-111.93, 116.45) * mm});
            skLineSegment(sketch, "E111.bottom", {"start": v(-88.26, 140.45) * mm, "end": v(-80.48, 140.45) * mm});
            skLineSegment(sketch, "E111.top", {"start": v(-88.26, 116.45) * mm, "end": v(-80.48, 116.45) * mm});
            skLineSegment(sketch, "E111.left", {"start": v(-88.26, 140.45) * mm, "end": v(-88.26, 136.39) * mm});
            skLineSegment(sketch, "E111.right", {"start": v(-80.48, 140.45) * mm, "end": v(-80.48, 116.45) * mm});
            skLineSegment(sketch, "E112.trimOffspring", {"start": v(-104.14, 120.51) * mm, "end": v(-104.14, 116.45) * mm});
            skLineSegment(sketch, "E113.trimOffspring", {"start": v(-88.26, 120.51) * mm, "end": v(-88.26, 116.45) * mm});
            skLineSegment(sketch, "E114", {"start": v(-104.14, 120.51) * mm, "end": v(-88.26, 120.51) * mm});
            skLineSegment(sketch, "E115", {"start": v(-103.5, 128.45) * mm, "end": v(-88.9, 128.45) * mm});
            skSolve(sketch);
        }
        {
            var Q0;
            Q0=makeQuery(id+"F49.opExtrude","CAP_FACE",FACE,{"disambiguationData":[OSD([sQuery(id+"F46.wireOp",EDGE,"837d0a8e-7aea-41cf-886a-b62b43243ce0"),sQuery(id+"F46.wireOp",EDGE,"d060f684-caa2-42fc-b72d-14a0c2717916"),sQuery(id+"F46.wireOp",EDGE,"17672764-d84c-446f-9bef-e2111f265863"),sQuery(id+"F46.wireOp",EDGE,"33cdaa7a-9be0-4ddf-9e29-9c811c9cda73"),sQuery(id+"F48.wireOp",EDGE,"E108")])],"isStart":true});
            cPlane(context, id + "F52", {"entities" : qUnion([Q0]), "cplaneType" : CPlaneType.OFFSET, "offset" : 6.35 * mm, "oppositeDirection" : true, "width" : 152.4 * mm, "height" : 152.4 * mm});
        }
        {
            var Q0;
            Q0=qCreatedBy(id+"F52.planeOp",FACE);
            var sketch = newSketch(context, id + "F53", { "sketchPlane" : qUnion([Q0])});
            skArc(sketch, "E116.0", {"start": v(128.45, 0) * mm, "mid": v(90.83, 90.83) * mm, "end": v(0, 128.45) * mm});
            skArc(sketch, "E117.0", {"start": v(-120.2, -729.4) * mm, "mid": v(-23.02, -901.07) * mm, "end": v(128.45, -774.7) * mm});
            skLineSegment(sketch, "E118", {"start": v(0, 0) * mm, "end": v(0, -774.7) * mm, "construction": true});
            skLineSegment(sketch, "E119", {"start": v(0, -387.35) * mm, "end": v(-127, -387.35) * mm, "construction": true});
            skLineSegment(sketch, "E120", {"start": v(0, -387.35) * mm, "end": v(127, -387.35) * mm, "construction": true});
            skArc(sketch, "E121", {"start": v(-8.16, -432.14) * mm, "mid": v(0, -387.35) * mm, "end": v(-8.16, -342.56) * mm});
            skLineSegment(sketch, "E122", {"start": v(-8.16, -342.56) * mm, "end": v(-120.2, -45.3) * mm});
            skLineSegment(sketch, "E123", {"start": v(-8.16, -432.14) * mm, "end": v(-120.2, -729.4) * mm});
            skLineSegment(sketch, "E124", {"start": v(0, 0) * mm, "end": v(0, 128.45) * mm, "construction": true});
            skPoint(sketch, "E124.endSnap0", {"position": v(0, 128.45) * mm});
            skPoint(sketch, "E125.orphan", {"position": v(0, 142.52) * mm});
            skLineSegment(sketch, "E126", {"start": v(0, 128.45) * mm, "end": v(0, 128.45) * mm});
            skArc(sketch, "E127", {"start": v(0, 128.45) * mm, "mid": v(-105.64, 73.08) * mm, "end": v(-120.2, -45.3) * mm});
            skLineSegment(sketch, "E128", {"start": v(128.45, 0) * mm, "end": v(128.45, -774.7) * mm});
            skSolve(sketch);
        }
        {
            var Q0;
            Q0=makeQuery(id+"F51.imprint","IMPRINT",FACE,{"disambiguationData":[TD([[makeQuery(id+"F51.imprint","IMPRINT",EDGE,{"derivedFrom":sQuery(id+"F51.wireOp",EDGE,"E109.top")}),-1.0]])]});
            var Q1;
            Q1=sQuery(id+"F53.wireOp",EDGE,"E116.0");
            var Q2;
            Q2=sQuery(id+"F53.wireOp",EDGE,"E128");
            var Q3;
            Q3=sQuery(id+"F53.wireOp",EDGE,"E117.0");
            var Q4;
            Q4=sQuery(id+"F53.wireOp",EDGE,"E123");
            var Q5;
            Q5=sQuery(id+"F53.wireOp",EDGE,"E121");
            var Q6;
            Q6=sQuery(id+"F53.wireOp",EDGE,"E122");
            var Q7;
            Q7=sQuery(id+"F53.wireOp",EDGE,"E127");
            sweep(context, id + "F54", {"profiles" : qUnion([Q0]), "path" : qUnion([Q1, Q2, Q3, Q4, Q5, Q6, Q7])});
        }
        {
            var Q0;
            Q0=makeQuery(id+"F1.opExtrude","CAP_FACE",FACE,{"disambiguationData":[OSD([sQuery(id+"F0.wireOp",EDGE,"E0.bottom"),sQuery(id+"F0.wireOp",EDGE,"E0.top"),sQuery(id+"F0.wireOp",EDGE,"E0.left"),sQuery(id+"F0.wireOp",EDGE,"E0.right"),sQuery(id+"F0.wireOp",EDGE,"E1"),sQuery(id+"F0.wireOp",EDGE,"E2")])],"isStart":true});
            var sketch = newSketch(context, id + "F55", { "sketchPlane" : qUnion([Q0])});
            skLineSegment(sketch, "E129", {"start": v(0, 0) * mm, "end": v(84.14, 84.14) * mm});
            skLineSegment(sketch, "E130", {"start": v(0, 0) * mm, "end": v(84.14, -84.14) * mm});
            skLineSegment(sketch, "E131", {"start": v(0, 0) * mm, "end": v(-84.14, -84.14) * mm});
            skLineSegment(sketch, "E132", {"start": v(0, 0) * mm, "end": v(-84.14, 84.14) * mm});
            skCircle(sketch, "E133", {"center": v(-84.14, 84.14) * mm, "radius": 33.33 * mm});
            skCircle(sketch, "E134", {"center": v(84.14, 84.14) * mm, "radius": 33.33 * mm});
            skCircle(sketch, "E135", {"center": v(84.14, -84.14) * mm, "radius": 33.33 * mm});
            skCircle(sketch, "E136", {"center": v(-84.14, -84.14) * mm, "radius": 33.33 * mm});
            skLineSegment(sketch, "E137.bottom", {"start": v(-76.2, 76.2) * mm, "end": v(76.2, 76.2) * mm});
            skLineSegment(sketch, "E137.top", {"start": v(-76.2, -76.2) * mm, "end": v(76.2, -76.2) * mm});
            skLineSegment(sketch, "E137.left", {"start": v(-76.2, 76.2) * mm, "end": v(-76.2, -76.2) * mm});
            skLineSegment(sketch, "E137.right", {"start": v(76.2, 76.2) * mm, "end": v(76.2, -76.2) * mm});
            skLineSegment(sketch, "E138", {"start": v(-60.58, 107.71) * mm, "end": v(107.71, -60.58) * mm});
            skLineSegment(sketch, "E139", {"start": v(-107.71, 60.58) * mm, "end": v(60.58, -107.71) * mm});
            skLineSegment(sketch, "E140", {"start": v(107.71, 60.58) * mm, "end": v(-60.58, -107.71) * mm});
            skLineSegment(sketch, "E141", {"start": v(60.58, 107.71) * mm, "end": v(-107.71, -60.58) * mm});
            skSolve(sketch);
        }
        {
            var Q0;
            {var subQ8=sQuery(id+"F55.wireOp",EDGE,"E133");var subQ10=makeQuery(id+"F55.imprint","INTERSECT",VERTEX,{"derivedFrom":[subQ8,sQuery(id+"F55.wireOp",EDGE,"E138")]});Q0=makeQuery(id+"F55.imprint","IMPRINT",FACE,{"disambiguationData":[TD([[makeQuery(id+"F55.imprint","IMPRINT",EDGE,{"disambiguationData":[TD([[subQ10,-1.0]])],"derivedFrom":subQ8}),1.0]])]});}
            var Q1;
            {var subQ2=sQuery(id+"F55.wireOp",EDGE,"E137.bottom");var subQ6=sQuery(id+"F55.wireOp",EDGE,"E133");var subQ8=makeQuery(id+"F55.imprint","INTERSECT",VERTEX,{"derivedFrom":[subQ6,subQ2]});Q1=makeQuery(id+"F55.imprint","IMPRINT",FACE,{"disambiguationData":[TD([[makeQuery(id+"F55.imprint","IMPRINT",EDGE,{"disambiguationData":[TD([[subQ8,1.0]])],"derivedFrom":subQ6}),1.0]])]});}
            var Q2;
            {var subQ2=sQuery(id+"F55.wireOp",EDGE,"E133");var subQ6=sQuery(id+"F55.wireOp",EDGE,"E137.left");var subQ8=makeQuery(id+"F55.imprint","INTERSECT",VERTEX,{"derivedFrom":[subQ2,subQ6]});Q2=makeQuery(id+"F55.imprint","IMPRINT",FACE,{"disambiguationData":[TD([[makeQuery(id+"F55.imprint","IMPRINT",EDGE,{"disambiguationData":[TD([[subQ8,-1.0]])],"derivedFrom":subQ2}),1.0]])]});}
            var Q3;
            {var subQ2=sQuery(id+"F55.wireOp",EDGE,"E133");var subQ11=sQuery(id+"F55.wireOp",EDGE,"E137.left");var subQ13=makeQuery(id+"F55.imprint","INTERSECT",VERTEX,{"derivedFrom":[subQ2,subQ11]});Q3=makeQuery(id+"F55.imprint","IMPRINT",FACE,{"disambiguationData":[TD([[makeQuery(id+"F55.imprint","IMPRINT",EDGE,{"disambiguationData":[TD([[subQ13,-1.0]])],"derivedFrom":subQ11}),1.0]])]});}
            var Q4;
            {var subQ0=sQuery(id+"F55.wireOp",EDGE,"E139");var subQ3=sQuery(id+"F55.wireOp",EDGE,"E133");var subQ4=makeQuery(id+"F55.imprint","INTERSECT",VERTEX,{"derivedFrom":[subQ3,subQ0]});Q4=makeQuery(id+"F55.imprint","IMPRINT",FACE,{"disambiguationData":[TD([[makeQuery(id+"F55.imprint","IMPRINT",EDGE,{"disambiguationData":[TD([[subQ4,-1.0]])],"derivedFrom":subQ3}),-1.0]])]});}
            var Q5;
            {var subQ2=sQuery(id+"F55.wireOp",EDGE,"E133");var subQ12=sQuery(id+"F55.wireOp",EDGE,"E137.bottom");var subQ14=makeQuery(id+"F55.imprint","INTERSECT",VERTEX,{"derivedFrom":[subQ2,subQ12]});Q5=makeQuery(id+"F55.imprint","IMPRINT",FACE,{"disambiguationData":[TD([[makeQuery(id+"F55.imprint","IMPRINT",EDGE,{"disambiguationData":[TD([[subQ14,-1.0]])],"derivedFrom":subQ12}),-1.0]])]});}
            var Q6;
            {var subQ0=sQuery(id+"F55.wireOp",EDGE,"E138");var subQ3=sQuery(id+"F55.wireOp",EDGE,"E133");var subQ4=makeQuery(id+"F55.imprint","INTERSECT",VERTEX,{"derivedFrom":[subQ3,subQ0]});Q6=makeQuery(id+"F55.imprint","IMPRINT",FACE,{"disambiguationData":[TD([[makeQuery(id+"F55.imprint","IMPRINT",EDGE,{"disambiguationData":[TD([[subQ4,1.0]])],"derivedFrom":subQ3}),-1.0]])]});}
            var Q7;
            {var subQ1=sQuery(id+"F55.wireOp",EDGE,"E141");var subQ3=sQuery(id+"F55.wireOp",EDGE,"E138");var subQ5=makeQuery(id+"F55.imprint","INTERSECT",VERTEX,{"derivedFrom":[subQ3,subQ1]});Q7=makeQuery(id+"F55.imprint","IMPRINT",FACE,{"disambiguationData":[TD([[makeQuery(id+"F55.imprint","IMPRINT",EDGE,{"disambiguationData":[TD([[subQ5,-1.0]])],"derivedFrom":subQ3}),-1.0]])]});}
            var Q8;
            {var subQ2=sQuery(id+"F55.wireOp",EDGE,"E134");var subQ9=sQuery(id+"F55.wireOp",EDGE,"E137.bottom");var subQ13=makeQuery(id+"F55.imprint","INTERSECT",VERTEX,{"derivedFrom":[subQ2,subQ9]});Q8=makeQuery(id+"F55.imprint","IMPRINT",FACE,{"disambiguationData":[TD([[makeQuery(id+"F55.imprint","IMPRINT",EDGE,{"disambiguationData":[TD([[subQ13,1.0]])],"derivedFrom":subQ9}),-1.0]])]});}
            var Q9;
            {var subQ1=sQuery(id+"F55.wireOp",EDGE,"E138");var subQ3=sQuery(id+"F55.wireOp",EDGE,"E137.bottom");var subQ5=makeQuery(id+"F55.imprint","INTERSECT",VERTEX,{"derivedFrom":[subQ3,subQ1]});Q9=makeQuery(id+"F55.imprint","IMPRINT",FACE,{"disambiguationData":[TD([[makeQuery(id+"F55.imprint","IMPRINT",EDGE,{"disambiguationData":[TD([[subQ5,-1.0]])],"derivedFrom":subQ3}),-1.0]])]});}
            var Q10;
            {var subQ2=sQuery(id+"F55.wireOp",EDGE,"E134");var subQ12=sQuery(id+"F55.wireOp",EDGE,"E137.right");var subQ14=makeQuery(id+"F55.imprint","INTERSECT",VERTEX,{"derivedFrom":[subQ2,subQ12]});Q10=makeQuery(id+"F55.imprint","IMPRINT",FACE,{"disambiguationData":[TD([[makeQuery(id+"F55.imprint","IMPRINT",EDGE,{"disambiguationData":[TD([[subQ14,-1.0]])],"derivedFrom":subQ12}),-1.0]])]});}
            var Q11;
            {var subQ0=sQuery(id+"F55.wireOp",EDGE,"E141");var subQ3=sQuery(id+"F55.wireOp",EDGE,"E134");var subQ4=makeQuery(id+"F55.imprint","INTERSECT",VERTEX,{"derivedFrom":[subQ3,subQ0]});Q11=makeQuery(id+"F55.imprint","IMPRINT",FACE,{"disambiguationData":[TD([[makeQuery(id+"F55.imprint","IMPRINT",EDGE,{"disambiguationData":[TD([[subQ4,-1.0]])],"derivedFrom":subQ3}),-1.0]])]});}
            var Q12;
            {var subQ8=sQuery(id+"F55.wireOp",EDGE,"E134");var subQ11=makeQuery(id+"F55.imprint","INTERSECT",VERTEX,{"derivedFrom":[subQ8,sQuery(id+"F55.wireOp",EDGE,"E141")]});Q12=makeQuery(id+"F55.imprint","IMPRINT",FACE,{"disambiguationData":[TD([[makeQuery(id+"F55.imprint","IMPRINT",EDGE,{"disambiguationData":[TD([[subQ11,-1.0]])],"derivedFrom":subQ8}),1.0]])]});}
            var Q13;
            {var subQ0=sQuery(id+"F55.wireOp",EDGE,"E140");var subQ3=sQuery(id+"F55.wireOp",EDGE,"E134");var subQ4=makeQuery(id+"F55.imprint","INTERSECT",VERTEX,{"derivedFrom":[subQ3,subQ0]});Q13=makeQuery(id+"F55.imprint","IMPRINT",FACE,{"disambiguationData":[TD([[makeQuery(id+"F55.imprint","IMPRINT",EDGE,{"disambiguationData":[TD([[subQ4,1.0]])],"derivedFrom":subQ3}),-1.0]])]});}
            var Q14;
            {var subQ2=sQuery(id+"F55.wireOp",EDGE,"E135");var subQ12=sQuery(id+"F55.wireOp",EDGE,"E137.right");var subQ14=makeQuery(id+"F55.imprint","INTERSECT",VERTEX,{"derivedFrom":[subQ2,subQ12]});Q14=makeQuery(id+"F55.imprint","IMPRINT",FACE,{"disambiguationData":[TD([[makeQuery(id+"F55.imprint","IMPRINT",EDGE,{"disambiguationData":[TD([[subQ14,1.0]])],"derivedFrom":subQ12}),-1.0]])]});}
            var Q15;
            {var subQ2=sQuery(id+"F55.wireOp",EDGE,"E135");var subQ11=sQuery(id+"F55.wireOp",EDGE,"E137.top");var subQ14=makeQuery(id+"F55.imprint","INTERSECT",VERTEX,{"derivedFrom":[subQ2,subQ11]});Q15=makeQuery(id+"F55.imprint","IMPRINT",FACE,{"disambiguationData":[TD([[makeQuery(id+"F55.imprint","IMPRINT",EDGE,{"disambiguationData":[TD([[subQ14,1.0]])],"derivedFrom":subQ11}),1.0]])]});}
            var Q16;
            {var subQ1=sQuery(id+"F55.wireOp",EDGE,"E140");var subQ3=sQuery(id+"F55.wireOp",EDGE,"E139");var subQ5=makeQuery(id+"F55.imprint","INTERSECT",VERTEX,{"derivedFrom":[subQ3,subQ1]});Q16=makeQuery(id+"F55.imprint","IMPRINT",FACE,{"disambiguationData":[TD([[makeQuery(id+"F55.imprint","IMPRINT",EDGE,{"disambiguationData":[TD([[subQ5,1.0]])],"derivedFrom":subQ3}),1.0]])]});}
            var Q17;
            {var subQ1=sQuery(id+"F55.wireOp",EDGE,"E141");var subQ3=sQuery(id+"F55.wireOp",EDGE,"E139");var subQ5=makeQuery(id+"F55.imprint","INTERSECT",VERTEX,{"derivedFrom":[subQ3,subQ1]});Q17=makeQuery(id+"F55.imprint","IMPRINT",FACE,{"disambiguationData":[TD([[makeQuery(id+"F55.imprint","IMPRINT",EDGE,{"disambiguationData":[TD([[subQ5,-1.0]])],"derivedFrom":subQ3}),1.0]])]});}
            var Q18;
            {var subQ8=sQuery(id+"F55.wireOp",EDGE,"E137.left");var subQ11=sQuery(id+"F55.wireOp",EDGE,"E136");var subQ14=makeQuery(id+"F55.imprint","INTERSECT",VERTEX,{"derivedFrom":[subQ11,subQ8]});Q18=makeQuery(id+"F55.imprint","IMPRINT",FACE,{"disambiguationData":[TD([[makeQuery(id+"F55.imprint","IMPRINT",EDGE,{"disambiguationData":[TD([[subQ14,1.0]])],"derivedFrom":subQ8}),1.0]])]});}
            var Q19;
            {var subQ2=sQuery(id+"F55.wireOp",EDGE,"E136");var subQ12=sQuery(id+"F55.wireOp",EDGE,"E137.top");var subQ14=makeQuery(id+"F55.imprint","INTERSECT",VERTEX,{"derivedFrom":[subQ2,subQ12]});Q19=makeQuery(id+"F55.imprint","IMPRINT",FACE,{"disambiguationData":[TD([[makeQuery(id+"F55.imprint","IMPRINT",EDGE,{"disambiguationData":[TD([[subQ14,-1.0]])],"derivedFrom":subQ12}),1.0]])]});}
            var Q20;
            {var subQ1=sQuery(id+"F55.wireOp",EDGE,"E140");var subQ3=sQuery(id+"F55.wireOp",EDGE,"E138");var subQ5=makeQuery(id+"F55.imprint","INTERSECT",VERTEX,{"derivedFrom":[subQ3,subQ1]});Q20=makeQuery(id+"F55.imprint","IMPRINT",FACE,{"disambiguationData":[TD([[makeQuery(id+"F55.imprint","IMPRINT",EDGE,{"disambiguationData":[TD([[subQ5,1.0]])],"derivedFrom":subQ3}),-1.0]])]});}
            var Q21;
            {var subQ0=sQuery(id+"F55.wireOp",EDGE,"E138");var subQ3=sQuery(id+"F55.wireOp",EDGE,"E135");var subQ4=makeQuery(id+"F55.imprint","INTERSECT",VERTEX,{"derivedFrom":[subQ3,subQ0]});Q21=makeQuery(id+"F55.imprint","IMPRINT",FACE,{"disambiguationData":[TD([[makeQuery(id+"F55.imprint","IMPRINT",EDGE,{"disambiguationData":[TD([[subQ4,-1.0]])],"derivedFrom":subQ3}),-1.0]])]});}
            var Q22;
            {var subQ0=sQuery(id+"F55.wireOp",EDGE,"E139");var subQ3=sQuery(id+"F55.wireOp",EDGE,"E135");var subQ4=makeQuery(id+"F55.imprint","INTERSECT",VERTEX,{"derivedFrom":[subQ3,subQ0]});Q22=makeQuery(id+"F55.imprint","IMPRINT",FACE,{"disambiguationData":[TD([[makeQuery(id+"F55.imprint","IMPRINT",EDGE,{"disambiguationData":[TD([[subQ4,1.0]])],"derivedFrom":subQ3}),-1.0]])]});}
            var Q23;
            {var subQ1=sQuery(id+"F55.wireOp",EDGE,"E140");var subQ3=sQuery(id+"F55.wireOp",EDGE,"E136");var subQ5=makeQuery(id+"F55.imprint","INTERSECT",VERTEX,{"derivedFrom":[subQ3,subQ1]});Q23=makeQuery(id+"F55.imprint","IMPRINT",FACE,{"disambiguationData":[TD([[makeQuery(id+"F55.imprint","IMPRINT",EDGE,{"disambiguationData":[TD([[subQ5,-1.0]])],"derivedFrom":subQ3}),-1.0]])]});}
            var Q24;
            {var subQ8=sQuery(id+"F55.wireOp",EDGE,"E136");var subQ12=makeQuery(id+"F55.imprint","INTERSECT",VERTEX,{"derivedFrom":[subQ8,sQuery(id+"F55.wireOp",EDGE,"E141")]});Q24=makeQuery(id+"F55.imprint","IMPRINT",FACE,{"disambiguationData":[TD([[makeQuery(id+"F55.imprint","IMPRINT",EDGE,{"disambiguationData":[TD([[subQ12,1.0]])],"derivedFrom":subQ8}),1.0]])]});}
            var Q25;
            {var subQ0=sQuery(id+"F55.wireOp",EDGE,"E141");var subQ3=sQuery(id+"F55.wireOp",EDGE,"E136");var subQ4=makeQuery(id+"F55.imprint","INTERSECT",VERTEX,{"derivedFrom":[subQ3,subQ0]});Q25=makeQuery(id+"F55.imprint","IMPRINT",FACE,{"disambiguationData":[TD([[makeQuery(id+"F55.imprint","IMPRINT",EDGE,{"disambiguationData":[TD([[subQ4,1.0]])],"derivedFrom":subQ3}),-1.0]])]});}
            var Q26;
            {var subQ2=sQuery(id+"F55.wireOp",EDGE,"E136");var subQ6=sQuery(id+"F55.wireOp",EDGE,"E137.top");var subQ8=makeQuery(id+"F55.imprint","INTERSECT",VERTEX,{"derivedFrom":[subQ2,subQ6]});Q26=makeQuery(id+"F55.imprint","IMPRINT",FACE,{"disambiguationData":[TD([[makeQuery(id+"F55.imprint","IMPRINT",EDGE,{"disambiguationData":[TD([[subQ8,-1.0]])],"derivedFrom":subQ2}),1.0]])]});}
            var Q27;
            {var subQ2=sQuery(id+"F55.wireOp",EDGE,"E135");var subQ6=sQuery(id+"F55.wireOp",EDGE,"E137.right");var subQ8=makeQuery(id+"F55.imprint","INTERSECT",VERTEX,{"derivedFrom":[subQ2,subQ6]});Q27=makeQuery(id+"F55.imprint","IMPRINT",FACE,{"disambiguationData":[TD([[makeQuery(id+"F55.imprint","IMPRINT",EDGE,{"disambiguationData":[TD([[subQ8,-1.0]])],"derivedFrom":subQ2}),1.0]])]});}
            var Q28;
            {var subQ8=sQuery(id+"F55.wireOp",EDGE,"E135");var subQ12=makeQuery(id+"F55.imprint","INTERSECT",VERTEX,{"derivedFrom":[subQ8,sQuery(id+"F55.wireOp",EDGE,"E138")]});Q28=makeQuery(id+"F55.imprint","IMPRINT",FACE,{"disambiguationData":[TD([[makeQuery(id+"F55.imprint","IMPRINT",EDGE,{"disambiguationData":[TD([[subQ12,-1.0]])],"derivedFrom":subQ8}),1.0]])]});}
            var Q29;
            {var subQ2=sQuery(id+"F55.wireOp",EDGE,"E137.top");var subQ6=sQuery(id+"F55.wireOp",EDGE,"E135");var subQ8=makeQuery(id+"F55.imprint","INTERSECT",VERTEX,{"derivedFrom":[subQ6,subQ2]});Q29=makeQuery(id+"F55.imprint","IMPRINT",FACE,{"disambiguationData":[TD([[makeQuery(id+"F55.imprint","IMPRINT",EDGE,{"disambiguationData":[TD([[subQ8,1.0]])],"derivedFrom":subQ6}),1.0]])]});}
            var Q30;
            {var subQ2=sQuery(id+"F55.wireOp",EDGE,"E137.left");var subQ6=sQuery(id+"F55.wireOp",EDGE,"E136");var subQ8=makeQuery(id+"F55.imprint","INTERSECT",VERTEX,{"derivedFrom":[subQ6,subQ2]});Q30=makeQuery(id+"F55.imprint","IMPRINT",FACE,{"disambiguationData":[TD([[makeQuery(id+"F55.imprint","IMPRINT",EDGE,{"disambiguationData":[TD([[subQ8,1.0]])],"derivedFrom":subQ6}),1.0]])]});}
            var Q31;
            {var subQ2=sQuery(id+"F55.wireOp",EDGE,"E137.right");var subQ6=sQuery(id+"F55.wireOp",EDGE,"E134");var subQ8=makeQuery(id+"F55.imprint","INTERSECT",VERTEX,{"derivedFrom":[subQ6,subQ2]});Q31=makeQuery(id+"F55.imprint","IMPRINT",FACE,{"disambiguationData":[TD([[makeQuery(id+"F55.imprint","IMPRINT",EDGE,{"disambiguationData":[TD([[subQ8,1.0]])],"derivedFrom":subQ6}),1.0]])]});}
            var Q32;
            {var subQ2=sQuery(id+"F55.wireOp",EDGE,"E134");var subQ6=sQuery(id+"F55.wireOp",EDGE,"E137.bottom");var subQ8=makeQuery(id+"F55.imprint","INTERSECT",VERTEX,{"derivedFrom":[subQ2,subQ6]});Q32=makeQuery(id+"F55.imprint","IMPRINT",FACE,{"disambiguationData":[TD([[makeQuery(id+"F55.imprint","IMPRINT",EDGE,{"disambiguationData":[TD([[subQ8,-1.0]])],"derivedFrom":subQ2}),1.0]])]});}
            var Q33;
            {var subQ1=sQuery(id+"F55.wireOp",EDGE,"E139");var subQ3=sQuery(id+"F55.wireOp",EDGE,"E137.left");var subQ5=makeQuery(id+"F55.imprint","INTERSECT",VERTEX,{"derivedFrom":[subQ3,subQ1]});Q33=makeQuery(id+"F55.imprint","IMPRINT",FACE,{"disambiguationData":[TD([[makeQuery(id+"F55.imprint","IMPRINT",EDGE,{"disambiguationData":[TD([[subQ5,-1.0]])],"derivedFrom":subQ3}),1.0]])]});}
            var Q34;
            {var subQ0=sQuery(id+"F55.wireOp",EDGE,"E140");var subQ3=sQuery(id+"F55.wireOp",EDGE,"E137.top");var subQ4=makeQuery(id+"F55.imprint","INTERSECT",VERTEX,{"derivedFrom":[subQ3,subQ0]});Q34=makeQuery(id+"F55.imprint","IMPRINT",FACE,{"disambiguationData":[TD([[makeQuery(id+"F55.imprint","IMPRINT",EDGE,{"disambiguationData":[TD([[subQ4,-1.0]])],"derivedFrom":subQ3}),1.0]])]});}
            var Q35;
            {var subQ0=sQuery(id+"F55.wireOp",EDGE,"E140");var subQ3=sQuery(id+"F55.wireOp",EDGE,"E137.right");var subQ4=makeQuery(id+"F55.imprint","INTERSECT",VERTEX,{"derivedFrom":[subQ3,subQ0]});Q35=makeQuery(id+"F55.imprint","IMPRINT",FACE,{"disambiguationData":[TD([[makeQuery(id+"F55.imprint","IMPRINT",EDGE,{"disambiguationData":[TD([[subQ4,-1.0]])],"derivedFrom":subQ3}),-1.0]])]});}
            extrude(context, id + "F56", {"entities" : qUnion([Q0, Q1, Q2, Q3, Q4, Q5, Q6, Q7, Q8, Q9, Q10, Q11, Q12, Q13, Q14, Q15, Q16, Q17, Q18, Q19, Q20, Q21, Q22, Q23, Q24, Q25, Q26, Q27, Q28, Q29, Q30, Q31, Q32, Q33, Q34, Q35]), "depth" : 22.22 * mm});
        }
        {
            var Q0;
            Q0=makeQuery(id+"F56.opExtrude","CAP_FACE",FACE,{"disambiguationData":[OSD([sQuery(id+"F0.wireOp",EDGE,"E0.bottom"),sQuery(id+"F0.wireOp",EDGE,"E0.top"),sQuery(id+"F0.wireOp",EDGE,"E0.left"),sQuery(id+"F0.wireOp",EDGE,"E0.right"),sQuery(id+"F0.wireOp",EDGE,"E1"),sQuery(id+"F0.wireOp",EDGE,"E2"),sQuery(id+"F2.wireOp",EDGE,"E12"),sQuery(id+"F2.wireOp",EDGE,"E13"),sQuery(id+"F2.wireOp",EDGE,"E14"),sQuery(id+"F2.wireOp",EDGE,"E15"),sQuery(id+"F2.wireOp",EDGE,"E16.1.0"),sQuery(id+"F2.wireOp",EDGE,"E16.1.1"),sQuery(id+"F2.wireOp",EDGE,"E16.1.2"),sQuery(id+"F2.wireOp",EDGE,"E16.1.3"),sQuery(id+"F2.wireOp",EDGE,"E16.2.0"),sQuery(id+"F2.wireOp",EDGE,"E16.2.1"),sQuery(id+"F2.wireOp",EDGE,"E16.2.2"),sQuery(id+"F2.wireOp",EDGE,"E16.2.3"),sQuery(id+"F2.wireOp",EDGE,"E16.3.0"),sQuery(id+"F2.wireOp",EDGE,"E16.3.1"),sQuery(id+"F2.wireOp",EDGE,"E16.3.2"),sQuery(id+"F2.wireOp",EDGE,"E16.3.3"),sQuery(id+"F55.wireOp",EDGE,"E133"),sQuery(id+"F55.wireOp",EDGE,"E134"),sQuery(id+"F55.wireOp",EDGE,"E135"),sQuery(id+"F55.wireOp",EDGE,"E136"),sQuery(id+"F55.wireOp",EDGE,"E137.bottom"),sQuery(id+"F55.wireOp",EDGE,"E137.top"),sQuery(id+"F55.wireOp",EDGE,"E137.left"),sQuery(id+"F55.wireOp",EDGE,"E137.right"),sQuery(id+"F55.wireOp",EDGE,"E138"),sQuery(id+"F55.wireOp",EDGE,"E139"),sQuery(id+"F55.wireOp",EDGE,"E140"),sQuery(id+"F55.wireOp",EDGE,"E141")])],"isStart":false});
            var sketch = newSketch(context, id + "F57", { "sketchPlane" : qUnion([Q0])});
            skCircle(sketch, "E142.0", {"center": v(0, 0) * mm, "radius": 31.75 * mm});
            skCircle(sketch, "E143", {"center": v(0, 0) * mm, "radius": 57.15 * mm});
            skSolve(sketch);
        }
        {
            var Q0;
            Q0=makeQuery(id+"F57.imprint","IMPRINT",FACE,{"disambiguationData":[TD([[makeQuery(id+"F57.imprint","IMPRINT",EDGE,{"derivedFrom":sQuery(id+"F57.wireOp",EDGE,"E142.0")}),1.0]])]});
            extrude(context, id + "F58", {"entities" : qUnion([Q0]), "operationType" : NewBodyOperationType.ADD, "depth" : 101.6 * mm});
        }
        {
            var Q0;
            Q0=makeQuery(id+"F58.opExtrude","CAP_FACE",FACE,{"disambiguationData":[OSD([sQuery(id+"F57.wireOp",EDGE,"E142.0"),sQuery(id+"F57.wireOp",EDGE,"E143")])],"isStart":false});
            var sketch = newSketch(context, id + "F59", { "sketchPlane" : qUnion([Q0])});
            skArc(sketch, "E144", {"start": v(133.48, 0) * mm, "mid": v(0, 133.48) * mm, "end": v(-133.48, 0) * mm});
            skLineSegment(sketch, "E145", {"start": v(-133.48, 0) * mm, "end": v(-133.48, -253.62) * mm});
            skLineSegment(sketch, "E146", {"start": v(-133.48, -253.62) * mm, "end": v(133.48, -253.62) * mm});
            skLineSegment(sketch, "E147", {"start": v(133.48, 0) * mm, "end": v(133.48, -253.62) * mm});
            skSolve(sketch);
        }
        {
            var Q0;
            Q0=makeQuery(id+"F1.opExtrude","SWEPT_FACE",FACE,{"disambiguationData":[OSD([sQuery(id+"F0.wireOp",EDGE,"E0.bottom")])]});
            cPlane(context, id + "F60", {"entities" : qUnion([Q0]), "cplaneType" : CPlaneType.OFFSET, "offset" : 222.95 * mm, "oppositeDirection" : true, "width" : 152.4 * mm, "height" : 152.4 * mm});
        }
        {
            var Q0;
            Q0=qCreatedBy(id+"F60.planeOp",FACE);
            var sketch = newSketch(context, id + "F61", { "sketchPlane" : qUnion([Q0])});
            skArc(sketch, "E148", {"start": v(-7.94, 144.08) * mm, "mid": v(0, 136.14) * mm, "end": v(7.94, 144.08) * mm});
            skLineSegment(sketch, "E149", {"start": v(-7.94, 144.08) * mm, "end": v(-7.94, 310.64) * mm});
            skLineSegment(sketch, "E150", {"start": v(-7.94, 310.64) * mm, "end": v(7.94, 310.64) * mm});
            skLineSegment(sketch, "E151", {"start": v(7.94, 144.08) * mm, "end": v(7.94, 310.64) * mm});
            skSolve(sketch);
        }
        {
            var Q0;
            Q0=makeQuery(id+"F61.imprint","IMPRINT",FACE,{"disambiguationData":[TD([[makeQuery(id+"F61.imprint","IMPRINT",EDGE,{"derivedFrom":sQuery(id+"F61.wireOp",EDGE,"E148")}),1.0]])]});
            extrude(context, id + "F62", {"entities" : qUnion([Q0]), "operationType" : NewBodyOperationType.REMOVE, "oppositeDirection" : true, "depth" : 8.25 * mm});
        }
        {
            var Q0;
            Q0=makeQuery(id+"F59.imprint","IMPRINT",FACE,{"disambiguationData":[TD([[makeQuery(id+"F59.imprint","IMPRINT",EDGE,{"derivedFrom":sQuery(id+"F59.wireOp",EDGE,"E144")}),1.0]])]});
            var Q1;
            Q1=makeQuery(id+"F59.imprint","IMPRINT",FACE,{"disambiguationData":[TD([[makeQuery(id+"F59.imprint","IMPRINT",EDGE,{"derivedFrom":makeQuery(id+"F58.opExtrude","CAP_EDGE",EDGE,{"disambiguationData":[OSD([sQuery(id+"F57.wireOp",EDGE,"E142.0")])],"isStart":false})}),1.0]])]});
            extrude(context, id + "F63", {"entities" : qUnion([Q0, Q1]), "operationType" : NewBodyOperationType.ADD, "depth" : 155.96 * mm});
        }
        {
            var Q0;
            Q0=makeQuery(id+"F63.opExtrude","SWEPT_EDGE",EDGE,{"disambiguationData":[OSD([sQuery(id+"F59.wireOp",EDGE,"E145"),sQuery(id+"F59.wireOp",EDGE,"E146")])]});
            var Q1;
            Q1=makeQuery(id+"F63.opExtrude","SWEPT_EDGE",EDGE,{"disambiguationData":[OSD([sQuery(id+"F59.wireOp",EDGE,"E146"),sQuery(id+"F59.wireOp",EDGE,"E147")])]});
            chamfer(context, id + "F64", {"entities" : qUnion([Q0, Q1]), "chamferType" : ChamferType.TWO_OFFSETS, "width1" : 76.2 * mm, "oppositeDirection" : false, "width2" : 38.1 * mm, "tangentPropagation" : true});
        }
        {
            var Q0;
            {var subQ0=sQuery(id+"F59.wireOp",EDGE,"E147");Q0=makeQuery(id+"F64.opChamfer","BLEND_EDGE",EDGE,{"blendedFrom":[makeQuery(id+"F63.opExtrude","SWEPT_EDGE",EDGE,{"disambiguationData":[OSD([sQuery(id+"F59.wireOp",EDGE,"E146"),subQ0])]}),makeQuery(id+"F63.opExtrude","SWEPT_FACE",FACE,{"disambiguationData":[OSD([subQ0])]})],"blendedInto":[makeQuery(id+"F63.opExtrude","SWEPT_FACE",FACE,{"disambiguationData":[OSD([subQ0])]})]});}
            var Q1;
            {var subQ0=sQuery(id+"F59.wireOp",EDGE,"E146");Q1=makeQuery(id+"F64.opChamfer","BLEND_EDGE",EDGE,{"blendedFrom":[makeQuery(id+"F63.opExtrude","SWEPT_EDGE",EDGE,{"disambiguationData":[OSD([subQ0,sQuery(id+"F59.wireOp",EDGE,"E147")])]}),makeQuery(id+"F63.opExtrude","SWEPT_FACE",FACE,{"disambiguationData":[OSD([subQ0])]})],"blendedInto":[makeQuery(id+"F63.opExtrude","SWEPT_FACE",FACE,{"disambiguationData":[OSD([subQ0])]})]});}
            var Q2;
            {var subQ0=sQuery(id+"F59.wireOp",EDGE,"E146");Q2=makeQuery(id+"F64.opChamfer","BLEND_EDGE",EDGE,{"blendedFrom":[makeQuery(id+"F63.opExtrude","SWEPT_EDGE",EDGE,{"disambiguationData":[OSD([sQuery(id+"F59.wireOp",EDGE,"E145"),subQ0])]}),makeQuery(id+"F63.opExtrude","SWEPT_FACE",FACE,{"disambiguationData":[OSD([subQ0])]})],"blendedInto":[makeQuery(id+"F63.opExtrude","SWEPT_FACE",FACE,{"disambiguationData":[OSD([subQ0])]})]});}
            var Q3;
            {var subQ0=sQuery(id+"F59.wireOp",EDGE,"E145");Q3=makeQuery(id+"F64.opChamfer","BLEND_EDGE",EDGE,{"blendedFrom":[makeQuery(id+"F63.opExtrude","SWEPT_EDGE",EDGE,{"disambiguationData":[OSD([subQ0,sQuery(id+"F59.wireOp",EDGE,"E146")])]}),makeQuery(id+"F63.opExtrude","SWEPT_FACE",FACE,{"disambiguationData":[OSD([subQ0])]})],"blendedInto":[makeQuery(id+"F63.opExtrude","SWEPT_FACE",FACE,{"disambiguationData":[OSD([subQ0])]})]});}
            fillet(context, id + "F65", {"entities" : qUnion([Q0, Q1, Q2, Q3]), "radius" : 25.4 * mm, "tangentPropagation" : true, "allowEdgeOverflow" : false});
        }
        {
            var Q0;
            Q0=makeQuery(id+"F63.opExtrude","CAP_EDGE",EDGE,{"disambiguationData":[OSD([sQuery(id+"F59.wireOp",EDGE,"E145")])],"isStart":false});
            var Q1;
            Q1=makeQuery(id+"F63.opExtrude","CAP_EDGE",EDGE,{"disambiguationData":[OSD([sQuery(id+"F59.wireOp",EDGE,"E144")])],"isStart":true});
            fillet(context, id + "F66", {"entities" : qUnion([Q0, Q1]), "radius" : 25.4 * mm, "tangentPropagation" : true, "allowEdgeOverflow" : false});
        }
        {
            var Q0;
            Q0=makeQuery(id+"F56.opExtrude","SWEPT_EDGE",EDGE,{"disambiguationData":[OSD([sQuery(id+"F55.wireOp",EDGE,"E137.right"),sQuery(id+"F55.wireOp",EDGE,"E138")])]});
            var Q1;
            Q1=makeQuery(id+"F56.opExtrude","SWEPT_EDGE",EDGE,{"disambiguationData":[OSD([sQuery(id+"F55.wireOp",EDGE,"E137.right"),sQuery(id+"F55.wireOp",EDGE,"E140")])]});
            var Q2;
            Q2=makeQuery(id+"F56.opExtrude","SWEPT_EDGE",EDGE,{"disambiguationData":[OSD([sQuery(id+"F55.wireOp",EDGE,"E137.top"),sQuery(id+"F55.wireOp",EDGE,"E140")])]});
            var Q3;
            Q3=makeQuery(id+"F56.opExtrude","SWEPT_EDGE",EDGE,{"disambiguationData":[OSD([sQuery(id+"F55.wireOp",EDGE,"E137.top"),sQuery(id+"F55.wireOp",EDGE,"E139")])]});
            var Q4;
            Q4=makeQuery(id+"F56.opExtrude","SWEPT_EDGE",EDGE,{"disambiguationData":[OSD([sQuery(id+"F55.wireOp",EDGE,"E137.left"),sQuery(id+"F55.wireOp",EDGE,"E141")])]});
            var Q5;
            Q5=makeQuery(id+"F56.opExtrude","SWEPT_EDGE",EDGE,{"disambiguationData":[OSD([sQuery(id+"F55.wireOp",EDGE,"E137.left"),sQuery(id+"F55.wireOp",EDGE,"E139")])]});
            var Q6;
            Q6=makeQuery(id+"F56.opExtrude","SWEPT_EDGE",EDGE,{"disambiguationData":[OSD([sQuery(id+"F55.wireOp",EDGE,"E137.bottom"),sQuery(id+"F55.wireOp",EDGE,"E141")])]});
            var Q7;
            Q7=makeQuery(id+"F56.opExtrude","SWEPT_EDGE",EDGE,{"disambiguationData":[OSD([sQuery(id+"F55.wireOp",EDGE,"E137.bottom"),sQuery(id+"F55.wireOp",EDGE,"E138")])]});
            fillet(context, id + "F67", {"entities" : qUnion([Q0, Q1, Q2, Q3, Q4, Q5, Q6, Q7]), "radius" : 25.4 * mm, "tangentPropagation" : true, "allowEdgeOverflow" : false});
        }
        {
            var Q0;
            {var subQ0=sQuery(id+"F55.wireOp",EDGE,"E137.bottom");var subQ1=sQuery(id+"F55.wireOp",EDGE,"E141");Q0=makeQuery(id+"F67.opFillet","BLEND_EDGE",EDGE,{"blendedFrom":[makeQuery(id+"F56.opExtrude","SWEPT_EDGE",EDGE,{"disambiguationData":[OSD([subQ0,subQ1])]}),makeQuery(id+"F56.opExtrude","CAP_FACE",FACE,{"disambiguationData":[OSD([sQuery(id+"F0.wireOp",EDGE,"E0.bottom"),sQuery(id+"F0.wireOp",EDGE,"E0.top"),sQuery(id+"F0.wireOp",EDGE,"E0.left"),sQuery(id+"F0.wireOp",EDGE,"E0.right"),sQuery(id+"F0.wireOp",EDGE,"E1"),sQuery(id+"F0.wireOp",EDGE,"E2"),sQuery(id+"F2.wireOp",EDGE,"E12"),sQuery(id+"F2.wireOp",EDGE,"E13"),sQuery(id+"F2.wireOp",EDGE,"E14"),sQuery(id+"F2.wireOp",EDGE,"E15"),sQuery(id+"F2.wireOp",EDGE,"E16.1.0"),sQuery(id+"F2.wireOp",EDGE,"E16.1.1"),sQuery(id+"F2.wireOp",EDGE,"E16.1.2"),sQuery(id+"F2.wireOp",EDGE,"E16.1.3"),sQuery(id+"F2.wireOp",EDGE,"E16.2.0"),sQuery(id+"F2.wireOp",EDGE,"E16.2.1"),sQuery(id+"F2.wireOp",EDGE,"E16.2.2"),sQuery(id+"F2.wireOp",EDGE,"E16.2.3"),sQuery(id+"F2.wireOp",EDGE,"E16.3.0"),sQuery(id+"F2.wireOp",EDGE,"E16.3.1"),sQuery(id+"F2.wireOp",EDGE,"E16.3.2"),sQuery(id+"F2.wireOp",EDGE,"E16.3.3"),sQuery(id+"F55.wireOp",EDGE,"E133"),sQuery(id+"F55.wireOp",EDGE,"E134"),sQuery(id+"F55.wireOp",EDGE,"E135"),sQuery(id+"F55.wireOp",EDGE,"E136"),subQ0,sQuery(id+"F55.wireOp",EDGE,"E137.top"),sQuery(id+"F55.wireOp",EDGE,"E137.left"),sQuery(id+"F55.wireOp",EDGE,"E137.right"),sQuery(id+"F55.wireOp",EDGE,"E138"),sQuery(id+"F55.wireOp",EDGE,"E139"),sQuery(id+"F55.wireOp",EDGE,"E140"),subQ1])],"isStart":false})],"blendedInto":[makeQuery(id+"F56.opExtrude","CAP_FACE",FACE,{"disambiguationData":[OSD([sQuery(id+"F0.wireOp",EDGE,"E0.bottom"),sQuery(id+"F0.wireOp",EDGE,"E0.top"),sQuery(id+"F0.wireOp",EDGE,"E0.left"),sQuery(id+"F0.wireOp",EDGE,"E0.right"),sQuery(id+"F0.wireOp",EDGE,"E1"),sQuery(id+"F0.wireOp",EDGE,"E2"),sQuery(id+"F2.wireOp",EDGE,"E12"),sQuery(id+"F2.wireOp",EDGE,"E13"),sQuery(id+"F2.wireOp",EDGE,"E14"),sQuery(id+"F2.wireOp",EDGE,"E15"),sQuery(id+"F2.wireOp",EDGE,"E16.1.0"),sQuery(id+"F2.wireOp",EDGE,"E16.1.1"),sQuery(id+"F2.wireOp",EDGE,"E16.1.2"),sQuery(id+"F2.wireOp",EDGE,"E16.1.3"),sQuery(id+"F2.wireOp",EDGE,"E16.2.0"),sQuery(id+"F2.wireOp",EDGE,"E16.2.1"),sQuery(id+"F2.wireOp",EDGE,"E16.2.2"),sQuery(id+"F2.wireOp",EDGE,"E16.2.3"),sQuery(id+"F2.wireOp",EDGE,"E16.3.0"),sQuery(id+"F2.wireOp",EDGE,"E16.3.1"),sQuery(id+"F2.wireOp",EDGE,"E16.3.2"),sQuery(id+"F2.wireOp",EDGE,"E16.3.3"),sQuery(id+"F55.wireOp",EDGE,"E133"),sQuery(id+"F55.wireOp",EDGE,"E134"),sQuery(id+"F55.wireOp",EDGE,"E135"),sQuery(id+"F55.wireOp",EDGE,"E136"),subQ0,sQuery(id+"F55.wireOp",EDGE,"E137.top"),sQuery(id+"F55.wireOp",EDGE,"E137.left"),sQuery(id+"F55.wireOp",EDGE,"E137.right"),sQuery(id+"F55.wireOp",EDGE,"E138"),sQuery(id+"F55.wireOp",EDGE,"E139"),sQuery(id+"F55.wireOp",EDGE,"E140"),subQ1])],"isStart":false})]});}
            fillet(context, id + "F68", {"entities" : qUnion([Q0]), "radius" : 6.35 * mm, "tangentPropagation" : true, "allowEdgeOverflow" : false});
        }
        {
            var Q0;
            Q0=makeQuery(id+"F58.opExtrude","CAP_EDGE",EDGE,{"disambiguationData":[OSD([sQuery(id+"F57.wireOp",EDGE,"E143")])],"isStart":true});
            var Q1;
            Q1=makeQuery(id+"F58.opExtrude","CAP_EDGE",EDGE,{"disambiguationData":[OSD([sQuery(id+"F57.wireOp",EDGE,"E143")])],"isStart":false});
            fillet(context, id + "F69", {"entities" : qUnion([Q0, Q1]), "radius" : 25.4 * mm, "tangentPropagation" : true, "allowEdgeOverflow" : false});
        }
        {
            var Q0;
            Q0=makeQuery(id+"F63.opExtrude","CAP_FACE",FACE,{"disambiguationData":[OSD([sQuery(id+"F57.wireOp",EDGE,"E142.0"),sQuery(id+"F59.wireOp",EDGE,"E144"),sQuery(id+"F59.wireOp",EDGE,"E145"),sQuery(id+"F59.wireOp",EDGE,"E146"),sQuery(id+"F59.wireOp",EDGE,"E147")])],"isStart":false});
            var sketch = newSketch(context, id + "F70", { "sketchPlane" : qUnion([Q0])});
            skCircle(sketch, "E152", {"center": v(70.1, -121.67) * mm, "radius": 18.26 * mm});
            skSolve(sketch);
        }
        {
            var Q0;
            Q0=makeQuery(id+"F70.imprint","IMPRINT",FACE,{"disambiguationData":[TD([[makeQuery(id+"F70.imprint","IMPRINT",EDGE,{"derivedFrom":sQuery(id+"F70.wireOp",EDGE,"E152")}),1.0]])]});
            extrude(context, id + "F71", {"entities" : qUnion([Q0]), "operationType" : NewBodyOperationType.ADD, "depth" : 141.48 * mm});
        }
        {
            var Q0;
            Q0=makeQuery(id+"F63.opExtrude","CAP_FACE",FACE,{"disambiguationData":[OSD([sQuery(id+"F57.wireOp",EDGE,"E142.0"),sQuery(id+"F59.wireOp",EDGE,"E144"),sQuery(id+"F59.wireOp",EDGE,"E145"),sQuery(id+"F59.wireOp",EDGE,"E146"),sQuery(id+"F59.wireOp",EDGE,"E147")])],"isStart":false});
            cPlane(context, id + "F72", {"entities" : qUnion([Q0]), "cplaneType" : CPlaneType.OFFSET, "offset" : 53.85 * mm, "width" : 152.4 * mm, "height" : 152.4 * mm});
        }
        {
            var Q0;
            Q0=qCreatedBy(id+"F72.planeOp",FACE);
            var sketch = newSketch(context, id + "F73", { "sketchPlane" : qUnion([Q0])});
            skLineSegment(sketch, "E153.bottom", {"start": v(298.7, -350.27) * mm, "end": v(-158.5, -350.27) * mm});
            skLineSegment(sketch, "E153.top", {"start": v(298.7, 741.93) * mm, "end": v(-158.5, 741.93) * mm});
            skLineSegment(sketch, "E153.left", {"start": v(298.7, -350.27) * mm, "end": v(298.7, 741.93) * mm});
            skLineSegment(sketch, "E153.right", {"start": v(-158.5, -350.27) * mm, "end": v(-158.5, 741.93) * mm});
            skCircle(sketch, "E154.0", {"center": v(70.1, -121.67) * mm, "radius": 18.26 * mm});
            skSolve(sketch);
        }
        {
            var Q0;
            Q0=makeQuery(id+"F73.imprint","IMPRINT",FACE,{"disambiguationData":[TD([[makeQuery(id+"F73.imprint","IMPRINT",EDGE,{"derivedFrom":sQuery(id+"F73.wireOp",EDGE,"E153.bottom")}),-1.0]])]});
            extrude(context, id + "F74", {"entities" : qUnion([Q0]), "depth" : 114.3 * mm});
        }
        {
            var Q0;
            Q0=makeQuery(id+"F1.opExtrude","SWEPT_FACE",FACE,{"disambiguationData":[OSD([sQuery(id+"F0.wireOp",EDGE,"E0.right")])]});
            cPlane(context, id + "F75", {"entities" : qUnion([Q0]), "cplaneType" : CPlaneType.OFFSET, "offset" : 12.7 * mm, "oppositeDirection" : true, "width" : 152.4 * mm, "height" : 152.4 * mm});
        }
        {
            var Q0;
            Q0=qCreatedBy(id+"F75.planeOp",FACE);
            var sketch = newSketch(context, id + "F76", { "sketchPlane" : qUnion([Q0])});
            skLineSegment(sketch, "E155.left", {"start": v(0, -469.9) * mm, "end": v(0, -12.7) * mm});
            skLineSegment(sketch, "E156", {"start": v(0, -12.7) * mm, "end": v(203.2, -469.9) * mm});
            skLineSegment(sketch, "E157", {"start": v(203.2, -469.9) * mm, "end": v(0, -469.9) * mm});
            skSolve(sketch);
        }
        {
            var Q0;
            Q0=makeQuery(id+"F76.imprint","IMPRINT",FACE,{"disambiguationData":[TD([[makeQuery(id+"F76.imprint","IMPRINT",EDGE,{"derivedFrom":sQuery(id+"F76.wireOp",EDGE,"E155.left")}),-1.0]])]});
            extrude(context, id + "F77", {"entities" : qUnion([Q0]), "oppositeDirection" : true, "depth" : 25.4 * mm});
        }
        {
            var Q0;
            Q0=makeQuery(id+"F1.opExtrude","SWEPT_FACE",FACE,{"disambiguationData":[OSD([sQuery(id+"F0.wireOp",EDGE,"E0.left")])]});
            cPlane(context, id + "F78", {"entities" : qUnion([Q0]), "cplaneType" : CPlaneType.OFFSET, "offset" : 12.7 * mm, "oppositeDirection" : true, "width" : 152.4 * mm, "height" : 152.4 * mm});
        }
        {
            var Q0;
            Q0=qCreatedBy(id+"F78.planeOp",FACE);
            var sketch = newSketch(context, id + "F79", { "sketchPlane" : qUnion([Q0])});
            skLineSegment(sketch, "E158.0.0", {"start": v(0, -469.9) * mm, "end": v(0, -12.7) * mm});
            skLineSegment(sketch, "E158.0.1", {"start": v(0, -12.7) * mm, "end": v(-203.2, -469.9) * mm});
            skLineSegment(sketch, "E158.0.2", {"start": v(-203.2, -469.9) * mm, "end": v(0, -469.9) * mm});
            skSolve(sketch);
        }
        {
            var Q0;
            Q0=makeQuery(id+"F79.imprint","IMPRINT",FACE,{"disambiguationData":[TD([[makeQuery(id+"F79.imprint","IMPRINT",EDGE,{"derivedFrom":sQuery(id+"F79.wireOp",EDGE,"E158.0.0")}),1.0]])]});
            extrude(context, id + "F80", {"entities" : qUnion([Q0]), "oppositeDirection" : true, "depth" : 25.4 * mm});
        }
        {
            var Q0;
            Q0=makeQuery(id+"F77.opExtrude","SWEPT_FACE",FACE,{"disambiguationData":[OSD([sQuery(id+"F76.wireOp",EDGE,"E155.left")])]});
            var sketch = newSketch(context, id + "F81", { "sketchPlane" : qUnion([Q0])});
            skArc(sketch, "E159.0", {"start": v(355.98, -152.4) * mm, "mid": v(349.25, -145.67) * mm, "end": v(342.52, -152.4) * mm});
            skArc(sketch, "E160.0", {"start": v(355.98, -355.6) * mm, "mid": v(349.25, -348.87) * mm, "end": v(342.52, -355.6) * mm});
            skArc(sketch, "E161.0", {"start": v(-342.52, -152.4) * mm, "mid": v(-349.25, -145.67) * mm, "end": v(-355.98, -152.4) * mm});
            skArc(sketch, "E162.0", {"start": v(-342.52, -355.6) * mm, "mid": v(-349.25, -348.87) * mm, "end": v(-355.98, -355.6) * mm});
            skSolve(sketch);
        }
        {
            var Q0;
            Q0=sQuery(id+"F81.wireOp",VERTEX,"E159.0.center");
            var Q1;
            Q1=sQuery(id+"F81.wireOp",VERTEX,"E160.0.center");
            var Q2;
            Q2=makeQuery(id+"F77.opExtrude","SWEPT_BODY",BODY,{"disambiguationData":[OSD([sQuery(id+"F76.wireOp",EDGE,"E155.left"),sQuery(id+"F76.wireOp",EDGE,"E156"),sQuery(id+"F76.wireOp",EDGE,"E157")])]});
            hole(context, id + "F82", {"style" : HoleStyle.SIMPLE, "holeDiameter" : 12.7 * mm, "endStyle" : HoleEndStyle.BLIND, "holeDepth" : 50.8 * mm, "locations" : qUnion([Q0, Q1]), "scope" : qUnion([Q2])});
        }
        {
            var Q0;
            Q0=sQuery(id+"F81.wireOp",VERTEX,"E161.0.center");
            var Q1;
            Q1=sQuery(id+"F81.wireOp",VERTEX,"E162.0.center");
            var Q2;
            Q2=makeQuery(id+"F80.opExtrude","SWEPT_BODY",BODY,{"disambiguationData":[OSD([sQuery(id+"F79.wireOp",EDGE,"E158.0.0"),sQuery(id+"F79.wireOp",EDGE,"E158.0.1"),sQuery(id+"F79.wireOp",EDGE,"E158.0.2")])]});
            hole(context, id + "F83", {"style" : HoleStyle.SIMPLE, "holeDiameter" : 12.7 * mm, "endStyle" : HoleEndStyle.BLIND, "holeDepth" : 50.8 * mm, "locations" : qUnion([Q0, Q1]), "scope" : qUnion([Q2])});
        }
        {
            var Q0;
            Q0=makeQuery(id+"F7.opExtrude","SWEPT_FACE",FACE,{"disambiguationData":[OSD([sQuery(id+"F5.wireOp",EDGE,"E36.bottom")])]});
            cPlane(context, id + "F84", {"entities" : qUnion([Q0]), "cplaneType" : CPlaneType.OFFSET, "offset" : 203.2 * mm, "width" : 152.4 * mm, "height" : 152.4 * mm});
        }
        {
            var Q0;
            Q0=qCreatedBy(id+"F84.planeOp",FACE);
            var sketch = newSketch(context, id + "F85", { "sketchPlane" : qUnion([Q0])});
            skLineSegment(sketch, "E163.0", {"start": v(336.55, 203.2) * mm, "end": v(361.95, 203.2) * mm});
            skLineSegment(sketch, "E164", {"start": v(349.25, 203.2) * mm, "end": v(349.25, 165.1) * mm, "construction": true});
            skLineSegment(sketch, "E165.0", {"start": v(-336.55, 203.2) * mm, "end": v(-361.95, 203.2) * mm});
            skLineSegment(sketch, "E166", {"start": v(-349.25, 203.2) * mm, "end": v(-349.25, 165.1) * mm, "construction": true});
            skLineSegment(sketch, "E167", {"start": v(336.55, 203.2) * mm, "end": v(336.55, 139.7) * mm});
            skLineSegment(sketch, "E168", {"start": v(336.55, 139.7) * mm, "end": v(361.95, 139.7) * mm});
            skLineSegment(sketch, "E169", {"start": v(361.95, 203.2) * mm, "end": v(361.95, 139.7) * mm});
            skLineSegment(sketch, "E170", {"start": v(-361.95, 203.2) * mm, "end": v(-361.95, 139.7) * mm});
            skLineSegment(sketch, "E171", {"start": v(-361.95, 139.7) * mm, "end": v(-336.55, 139.7) * mm});
            skLineSegment(sketch, "E172", {"start": v(-336.55, 203.2) * mm, "end": v(-336.55, 139.7) * mm});
            skSolve(sketch);
        }
        {
            var Q0;
            Q0=sQuery(id+"F85.wireOp",VERTEX,"E166.end");
            var Q1;
            Q1=sQuery(id+"F85.wireOp",VERTEX,"E164.end");
            var Q2;
            Q2=makeQuery(id+"F77.opExtrude","SWEPT_BODY",BODY,{"disambiguationData":[OSD([sQuery(id+"F76.wireOp",EDGE,"E155.left"),sQuery(id+"F76.wireOp",EDGE,"E156"),sQuery(id+"F76.wireOp",EDGE,"E157")])]});
            var Q3;
            Q3=makeQuery(id+"F80.opExtrude","SWEPT_BODY",BODY,{"disambiguationData":[OSD([sQuery(id+"F79.wireOp",EDGE,"E158.0.0"),sQuery(id+"F79.wireOp",EDGE,"E158.0.1"),sQuery(id+"F79.wireOp",EDGE,"E158.0.2")])]});
            hole(context, id + "F86", {"style" : HoleStyle.SIMPLE, "holeDiameter" : 13.46 * mm, "endStyle" : HoleEndStyle.BLIND, "holeDepth" : 304.8 * mm, "locations" : qUnion([Q0, Q1]), "scope" : qUnion([Q2, Q3])});
        }
        {
            var Q0;
            Q0=makeQuery(id+"F85.imprint","IMPRINT",FACE,{"disambiguationData":[TD([[makeQuery(id+"F85.imprint","IMPRINT",EDGE,{"derivedFrom":sQuery(id+"F85.wireOp",EDGE,"E165.0")}),1.0]])]});
            var Q1;
            Q1=makeQuery(id+"F85.imprint","IMPRINT",FACE,{"disambiguationData":[TD([[makeQuery(id+"F85.imprint","IMPRINT",EDGE,{"derivedFrom":sQuery(id+"F85.wireOp",EDGE,"E163.0")}),-1.0]])]});
            extrude(context, id + "F87", {"entities" : qUnion([Q0, Q1]), "operationType" : NewBodyOperationType.REMOVE, "oppositeDirection" : true, "depth" : 152.4 * mm});
        }
        {
            var Q0;
            Q0=makeQuery(id+"F39.opRevolve","SWEPT_EDGE",EDGE,{"disambiguationData":[OSD([sQuery(id+"F38.wireOp",EDGE,"E92.bottom"),sQuery(id+"F38.wireOp",EDGE,"E92.right")])]});
            var Q1;
            Q1=makeQuery(id+"F39.opRevolve","SWEPT_EDGE",EDGE,{"disambiguationData":[OSD([sQuery(id+"F38.wireOp",EDGE,"E91.top"),sQuery(id+"F38.wireOp",EDGE,"E94")])]});
            var Q2;
            Q2=makeQuery(id+"F39.opRevolve","SWEPT_EDGE",EDGE,{"disambiguationData":[OSD([sQuery(id+"F38.wireOp",EDGE,"E90.top"),sQuery(id+"F38.wireOp",EDGE,"E90.left")])]});
            var Q3;
            Q3=makeQuery(id+"F11.opExtrude","CAP_EDGE",EDGE,{"disambiguationData":[OSD([sQuery(id+"F10.wireOp",EDGE,"E49")])],"isStart":false});
            var Q4;
            Q4=makeQuery(id+"F15.opExtrude","CAP_EDGE",EDGE,{"disambiguationData":[OSD([sQuery(id+"F10.wireOp",EDGE,"E49")])],"isStart":false});
            chamfer(context, id + "F88", {"entities" : qUnion([Q0, Q1, Q2, Q3, Q4]), "width" : 0.76 * mm, "tangentPropagation" : true});
        }
        {
            var Q0;
            Q0=makeQuery(id+"F39.opRevolve","SWEPT_EDGE",EDGE,{"disambiguationData":[OSD([sQuery(id+"F38.wireOp",EDGE,"E90.top"),sQuery(id+"F38.wireOp",EDGE,"E94")])]});
            fillet(context, id + "F89", {"entities" : qUnion([Q0]), "radius" : 0.76 * mm, "tangentPropagation" : true, "allowEdgeOverflow" : false});
        }
        {
            var Q0;
            Q0=sQuery(id+"F21.wireOp",VERTEX,"E56.end");
            var Q1;
            Q1=makeQuery(id+"F20.opExtrude","SWEPT_BODY",BODY,{"disambiguationData":[OSD([sQuery(id+"F19.wireOp",EDGE,"E54"),sQuery(id+"F19.wireOp",EDGE,"E55.0")])]});
            var Q2;
            Q2=makeQuery(id+"F11.opExtrude","SWEPT_BODY",BODY,{"disambiguationData":[OSD([sQuery(id+"F10.wireOp",EDGE,"E49")])]});
            hole(context, id + "F90", {"style" : HoleStyle.SIMPLE, "holeDiameter" : 16.67 * mm, "endStyle" : HoleEndStyle.BLIND, "holeDepth" : 254 * mm, "locations" : qUnion([Q0]), "scope" : qUnion([Q1, Q2])});
        }
        {
            var Q0;
            Q0=sQuery(id+"F22.wireOp",VERTEX,"E59.end");
            var Q1;
            Q1=makeQuery(id+"F20.opExtrude","SWEPT_BODY",BODY,{"disambiguationData":[OSD([sQuery(id+"F19.wireOp",EDGE,"E54"),sQuery(id+"F19.wireOp",EDGE,"E55.0")])]});
            var Q2;
            Q2=makeQuery(id+"F11.opExtrude","SWEPT_BODY",BODY,{"disambiguationData":[OSD([sQuery(id+"F10.wireOp",EDGE,"E49")])]});
            hole(context, id + "F91", {"style" : HoleStyle.SIMPLE, "holeDiameter" : 16.67 * mm, "endStyle" : HoleEndStyle.BLIND, "holeDepth" : 254 * mm, "locations" : qUnion([Q0]), "scope" : qUnion([Q1, Q2])});
        }
    });
